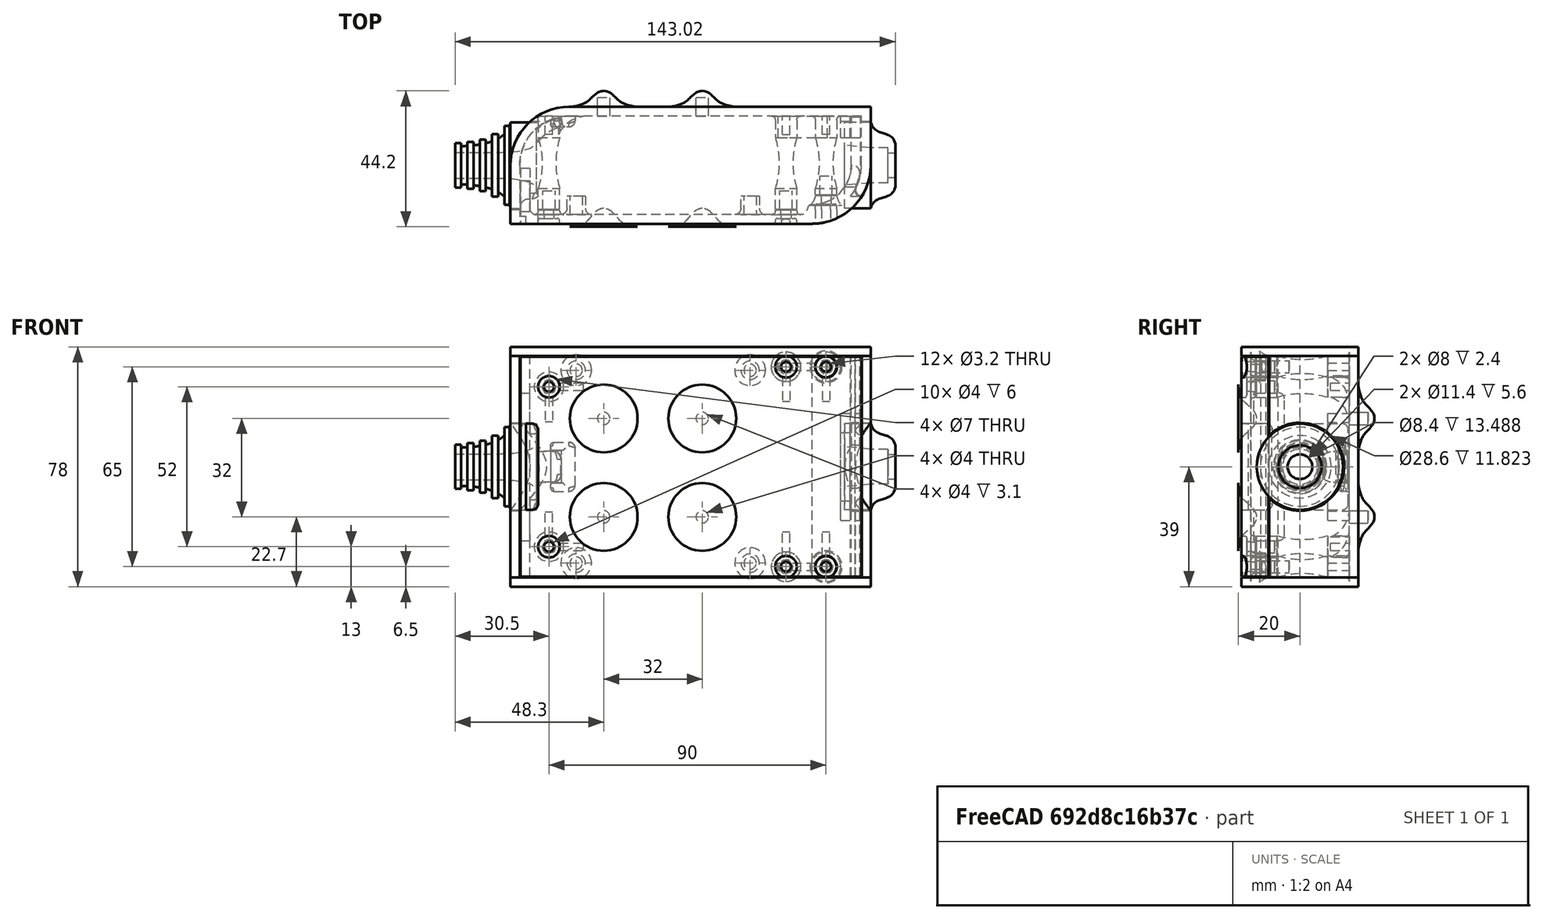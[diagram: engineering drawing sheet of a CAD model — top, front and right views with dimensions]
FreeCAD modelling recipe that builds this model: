
FCSTD DOCUMENT  (FreeCAD 0.19R0.19.2)
Label: enclosure_095
License: All rights reserved
LicenseURL: http://en.wikipedia.org/wiki/All_rights_reserved
objects: Part::Feature×72, Part::Revolution×72, Part::MultiFuse×52, Sketcher::SketchObject×29, Part::Fillet×22, Part::Cylinder×22, Part::Cut×19, Part::Extrusion×18, Part::Box×12, App::MeasureDistance×3
note: 318 computed .brp shape members not serialized (recipe doc carries the construction recipe); baked Part::Feature solids carry a one-line shape summary decoded from their .brp

FEATURE [Sketcher::SketchObject] Sketch  label="topSketch"
  FullyConstrained = true
  sketch-geometry (13):
    g0: LineSegment StartX=117 StartY=19 StartZ=0 EndX=117 EndY=38 EndZ=0
    g1: ArcOfCircle CenterX=98 CenterY=19 CenterZ=0 NormalX=0 NormalY=0 NormalZ=1 AngleXU=0 Radius=19 StartAngle=5.7297 EndAngle=6.28319
    g2: LineSegment StartX=0 StartY=3 StartZ=0 EndX=0 EndY=19 EndZ=0
    g3: LineSegment StartX=19 StartY=38 StartZ=0 EndX=117 EndY=38 EndZ=0
    g4: ArcOfCircle CenterX=19 CenterY=19 CenterZ=0 NormalX=0 NormalY=0 NormalZ=1 AngleXU=0 Radius=19 StartAngle=1.5708 EndAngle=3.14159
    g5: ArcOfCircle CenterX=19 CenterY=19 CenterZ=0 NormalX=0 NormalY=0 NormalZ=1 AngleXU=0 Radius=16 StartAngle=1.5708 EndAngle=3.14159
    g6: ArcOfCircle CenterX=98 CenterY=19 CenterZ=0 NormalX=0 NormalY=0 NormalZ=1 AngleXU=0 Radius=16 StartAngle=5.60905 EndAngle=6.28319
    g7: LineSegment StartX=114 StartY=19 StartZ=0 EndX=114 EndY=35 EndZ=0
    g8: LineSegment StartX=110.5 StartY=9.01251 StartZ=0 EndX=114.163 EndY=9.01251 EndZ=0
    g9: LineSegment StartX=114 StartY=35 StartZ=0 EndX=19 EndY=35 EndZ=0
    g10: LineSegment StartX=0 StartY=3 StartZ=0 EndX=0 EndY=0 EndZ=0
    g11: LineSegment StartX=3 StartY=0 StartZ=0 EndX=0 EndY=0 EndZ=0
    g12: LineSegment StartX=3 StartY=19 StartZ=0 EndX=3 EndY=0 EndZ=0
  constraints (33):
    c: Vertical(g0)
    c: Distance(g0) = 19
    c: Block(g0)
    c: Coincident(g1,g0)
    c: Block(g1)
    c: Vertical(g2)
    c: Block(g2)
    c: Coincident(g3,g0)
    c: Horizontal(g3)
    c: Distance(g3) = 98
    c: Coincident(g4,g3)
    c: Coincident(g4,g2)
    c: Block(g4)
    c: Coincident(g5,g4)
    c: Coincident(g6,g1)
    c: Block(g6)
    c: Block(g5)
    c: Coincident(g7,g6)
    c: Vertical(g7)
    c: Coincident(g8,g6)
    c: Coincident(g8,g1)
    c: Coincident(g9,g7)
    c: Coincident(g9,g5)
    c: Horizontal(g9)
    c: Tangent(g9,g5)
    c: Coincident(g10,g2)
    c: Distance(g10) = 3
    c: Vertical(g10)
    c: Coincident(g11,g10)
    c: Horizontal(g11)
    c: Coincident(g12,g5)
    c: Coincident(g12,g11)
    c: Vertical(g12)
FEATURE [Sketcher::SketchObject] Sketch001  label="bottomSketch"
  FullyConstrained = true
  sketch-geometry (32):
    g0: LineSegment StartX=3.3 StartY=-6.03275e-07 StartZ=0 EndX=98 EndY=-6.03275e-07 EndZ=0
    g1: ArcOfCircle CenterX=98 CenterY=19 CenterZ=0 NormalX=0 NormalY=0 NormalZ=1 AngleXU=0 Radius=19 StartAngle=4.71239 EndAngle=5.71103
    g2: LineSegment StartX=6.3 StartY=8 StartZ=0 EndX=3.3 EndY=8 EndZ=0
    g3: LineSegment StartX=3.3 StartY=8 StartZ=0 EndX=3.3 EndY=-6.03275e-07 EndZ=0
    g4: ArcOfCircle CenterX=8.3 CenterY=5 CenterZ=0 NormalX=0 NormalY=0 NormalZ=1 AngleXU=0 Radius=2 StartAngle=3.14159 EndAngle=4.71239
    g5: LineSegment StartX=6.3 StartY=8 StartZ=0 EndX=6.3 EndY=5 EndZ=0
    g6: ArcOfCircle CenterX=98 CenterY=19 CenterZ=0 NormalX=0 NormalY=0 NormalZ=1 AngleXU=0 Radius=12.7 StartAngle=4.71239 EndAngle=6.28319
    g7: LineSegment StartX=94.7 StartY=3 StartZ=0 EndX=8.3 EndY=3 EndZ=0
    g8-g12: Circle x5 (B-spline internal-alignment scaffolding for g13; pole/knot coordinates omitted)
    g13: BSplineCurve PolesCount=5 KnotsCount=3 Degree=3 IsPeriodic=0
    g14: GeomPoint X=98 Y=6.3 Z=0
    g15: GeomPoint X=96.3938 Y=4.71946 Z=0
    g16: GeomPoint X=94.7 Y=3 Z=0
    g17-g23: Circle x7 (B-spline internal-alignment scaffolding for g24; pole/knot coordinates omitted)
    g24: BSplineCurve PolesCount=7 KnotsCount=5 Degree=3 IsPeriodic=0
    g25-g29: GeomPoint x5 (B-spline internal-alignment scaffolding for g24; pole/knot coordinates omitted)
    g30: ArcOfCircle CenterX=98 CenterY=19 CenterZ=0 NormalX=0 NormalY=0 NormalZ=1 AngleXU=0 Radius=15.7 StartAngle=5.81226 EndAngle=6.28319
    g31: LineSegment StartX=110.7 StartY=19 StartZ=0 EndX=113.7 EndY=19 EndZ=0
  constraints (41):
    c: Horizontal(g0)
    c: Coincident(g1,g0)
    c: Block(g1)
    c: Horizontal(g2)
    c: Distance(g2) = 3
    c: Coincident(g3,g2)
    c: Vertical(g3)
    c: Coincident(g3,g0)
    c: Block(g4)
    c: Block(g2)
    c: Coincident(g5,g2)
    c: Coincident(g5,g4)
    c: Vertical(g5)
    c: Coincident(g6,g1)
    c: Block(g6)
    c: Coincident(g7,g4)
    c: Horizontal(g7)
    c: Block(g0)
    c: Block(g7)
    c: Block(g3)
    c: Coincident(g13,g6)
    c: Weight(g8) = 1
    c: Equal(g8, g9-g12) x4
    c: Coincident(g13,g7)
    c: InternalAlignment(g8-g12 -> g13) x5
    c: InternalAlignment(g14,g13)
    c: InternalAlignment(g15,g13)
    c: InternalAlignment(g16,g13)
    c: Block(g13)
    c: Weight(g17) = 1
    c: Equal(g17, g18-g23) x6
    c: Coincident(g24,g1)
    c: InternalAlignment(g17-g23 -> g24) x7
    c: InternalAlignment(g25-g29 -> g24) x5
    c: Block(g24)
    c: Coincident(g30,g24)
    c: Coincident(g31,g6)
    c: Coincident(g31,g30)
    c: Horizontal(g31)
    c: Block(g31)
    c: Block(g30)
FEATURE [Part::Extrusion] Extrude  label="top"
  Base = -> Sketch
  Dir = (0,0,1)
  DirMode = 2
  FaceMakerClass = Part::FaceMakerBullseye
  LengthFwd = 72
  LengthRev = 0
  Solid = true
  Symmetric = false
FEATURE [Part::Extrusion] Extrude001  label="bottom"
  Base = -> Sketch001
  Dir = (0,0,1)
  DirMode = 2
  FaceMakerClass = Part::FaceMakerBullseye
  LengthFwd = 71.4
  LengthRev = 0
  Placement = pos=(0,0,0.3) rot=(0,0,1;0rad)
  Solid = true
  Symmetric = false
FEATURE [Sketcher::SketchObject] Sketch002  label="topSketch001"
  FullyConstrained = true
  sketch-geometry (6):
    g0: LineSegment StartX=19 StartY=38 StartZ=0 EndX=117 EndY=38 EndZ=0
    g1: ArcOfCircle CenterX=19 CenterY=19 CenterZ=0 NormalX=0 NormalY=0 NormalZ=1 AngleXU=0 Radius=19 StartAngle=1.5708 EndAngle=3.14159
    g2: LineSegment StartX=117 StartY=38 StartZ=0 EndX=117 EndY=19 EndZ=0
    g3: LineSegment StartX=98 StartY=1.0161e-12 StartZ=0 EndX=5.22862e-06 EndY=1.0161e-12 EndZ=0
    g4: LineSegment StartX=5.22862e-06 StartY=19 StartZ=0 EndX=5.22862e-06 EndY=1.0161e-12 EndZ=0
    g5: ArcOfCircle CenterX=98 CenterY=19 CenterZ=0 NormalX=0 NormalY=0 NormalZ=1 AngleXU=0 Radius=19 StartAngle=4.71239 EndAngle=6.28319
  constraints (16):
    c: Horizontal(g0)
    c: Distance(g0) = 98
    c: Coincident(g1,g0)
    c: Block(g1)
    c: Coincident(g2,g0)
    c: Vertical(g2)
    c: Distance(g2) = 19
    c: Horizontal(g3)
    c: Coincident(g4,g1)
    c: Vertical(g4)
    c: Coincident(g3,g4)
    c: Block(g3)
    c: Coincident(g5,g2)
    c: Coincident(g5,g3)
    c: Block(g0)
    c: Block(g5)
FEATURE [Part::Extrusion] Extrude002  label="sideA"
  Base = -> Sketch002
  Dir = (0,0,1)
  DirMode = 2
  FaceMakerClass = Part::FaceMakerBullseye
  LengthFwd = 3
  LengthRev = 0
  Placement = pos=(0,0,-3) rot=(0,0,1;0rad)
  Solid = true
  Symmetric = false
FEATURE [Sketcher::SketchObject] Sketch003  label="topSketch002"
  FullyConstrained = true
  sketch-geometry (6):
    g0: LineSegment StartX=19 StartY=38 StartZ=0 EndX=117 EndY=38 EndZ=0
    g1: ArcOfCircle CenterX=19 CenterY=19 CenterZ=0 NormalX=0 NormalY=0 NormalZ=1 AngleXU=0 Radius=19 StartAngle=1.5708 EndAngle=3.14159
    g2: LineSegment StartX=117 StartY=38 StartZ=0 EndX=117 EndY=19 EndZ=0
    g3: LineSegment StartX=98 StartY=1.0161e-12 StartZ=0 EndX=5.22862e-06 EndY=1.0161e-12 EndZ=0
    g4: LineSegment StartX=5.22862e-06 StartY=19 StartZ=0 EndX=5.22862e-06 EndY=1.0161e-12 EndZ=0
    g5: ArcOfCircle CenterX=98 CenterY=19 CenterZ=0 NormalX=0 NormalY=0 NormalZ=1 AngleXU=0 Radius=19 StartAngle=4.71239 EndAngle=6.28319
  constraints (16):
    c: Horizontal(g0)
    c: Distance(g0) = 98
    c: Coincident(g1,g0)
    c: Block(g1)
    c: Coincident(g2,g0)
    c: Vertical(g2)
    c: Distance(g2) = 19
    c: Horizontal(g3)
    c: Coincident(g4,g1)
    c: Vertical(g4)
    c: Coincident(g3,g4)
    c: Block(g3)
    c: Coincident(g5,g2)
    c: Coincident(g5,g3)
    c: Block(g0)
    c: Block(g5)
FEATURE [Part::Extrusion] Extrude003  label="sideB"
  Base = -> Sketch003
  Dir = (0,0,1)
  DirMode = 2
  FaceMakerClass = Part::FaceMakerBullseye
  LengthFwd = 3
  LengthRev = 0
  Placement = pos=(0,0,72) rot=(0,0,1;0rad)
  Solid = true
  Symmetric = false
FEATURE [Sketcher::SketchObject] Sketch004
  FullyConstrained = true
  MapMode = 3
  Placement = pos=(0,0,0) rot=(1,0,0;1.5708rad)
  Support = -> [Extrude]
  sketch-geometry (8):
    g0: Circle CenterX=80.351 CenterY=-67.6202 CenterZ=0 NormalX=0 NormalY=0 NormalZ=1 AngleXU=0 Radius=2
    g1: Circle CenterX=80.351 CenterY=-67.6202 CenterZ=0 NormalX=0 NormalY=0 NormalZ=1 AngleXU=0 Radius=3
    g2: Circle CenterX=80.351 CenterY=-4.92017 CenterZ=0 NormalX=0 NormalY=0 NormalZ=1 AngleXU=0 Radius=2
    g3: Circle CenterX=80.351 CenterY=-4.92017 CenterZ=0 NormalX=0 NormalY=0 NormalZ=1 AngleXU=0 Radius=3
    g4: Circle CenterX=23.851 CenterY=-4.92017 CenterZ=0 NormalX=0 NormalY=0 NormalZ=1 AngleXU=0 Radius=2
    g5: Circle CenterX=23.851 CenterY=-4.92017 CenterZ=0 NormalX=0 NormalY=0 NormalZ=1 AngleXU=0 Radius=3
    g6: Circle CenterX=23.851 CenterY=-67.6202 CenterZ=0 NormalX=0 NormalY=0 NormalZ=1 AngleXU=0 Radius=2
    g7: Circle CenterX=23.851 CenterY=-67.6202 CenterZ=0 NormalX=0 NormalY=0 NormalZ=1 AngleXU=0 Radius=3
  constraints (8):
    c: Block(g3)
    c: Block(g2)
    c: Block(g1)
    c: Block(g0)
    c: Block(g6)
    c: Block(g7)
    c: Block(g4)
    c: Block(g5)
FEATURE [Part::Extrusion] Extrude004
  Base = -> Sketch004
  Dir = (0,-1,2e-16)
  DirMode = 2
  FaceMakerClass = Part::FaceMakerBullseye
  LengthFwd = 6
  LengthRev = 0
  Placement = pos=(0,9,0) rot=(0,0,1;0rad)
  Solid = true
  Symmetric = false
FEATURE [Sketcher::SketchObject] Sketch005
  FullyConstrained = true
  MapMode = 3
  Placement = pos=(0,0,0) rot=(1,0,0;1.5708rad)
  Support = -> [Extrude]
  sketch-geometry (8):
    g0: Circle CenterX=80.351 CenterY=-67.6202 CenterZ=0 NormalX=0 NormalY=0 NormalZ=1 AngleXU=0 Radius=3
    g1: Circle CenterX=80.351 CenterY=-4.92017 CenterZ=0 NormalX=0 NormalY=0 NormalZ=1 AngleXU=0 Radius=3
    g2: Circle CenterX=23.851 CenterY=-4.92017 CenterZ=0 NormalX=0 NormalY=0 NormalZ=1 AngleXU=0 Radius=3
    g3: Circle CenterX=23.851 CenterY=-67.6202 CenterZ=0 NormalX=0 NormalY=0 NormalZ=1 AngleXU=0 Radius=3
    g4: Circle CenterX=23.851 CenterY=-67.6202 CenterZ=0 NormalX=0 NormalY=0 NormalZ=1 AngleXU=0 Radius=5
    g5: Circle CenterX=80.351 CenterY=-67.6202 CenterZ=0 NormalX=0 NormalY=0 NormalZ=1 AngleXU=0 Radius=5
    g6: Circle CenterX=23.851 CenterY=-4.92017 CenterZ=0 NormalX=0 NormalY=0 NormalZ=1 AngleXU=0 Radius=5
    g7: Circle CenterX=80.351 CenterY=-4.92017 CenterZ=0 NormalX=0 NormalY=0 NormalZ=1 AngleXU=0 Radius=5
  constraints (8):
    c: Block(g1)
    c: Block(g0)
    c: Block(g3)
    c: Block(g2)
    c: Block(g5)
    c: Block(g4)
    c: Block(g6)
    c: Block(g7)
FEATURE [Part::Extrusion] Extrude005
  Base = -> Sketch005
  Dir = (0,-1,2e-16)
  DirMode = 2
  FaceMakerClass = Part::FaceMakerBullseye
  LengthFwd = 2
  LengthRev = 0
  Solid = true
  Symmetric = false
FEATURE [Sketcher::SketchObject] Sketch006
  FullyConstrained = true
  MapMode = 3
  Placement = pos=(0,0,0) rot=(1,0,0;1.5708rad)
  sketch-geometry (8):
    g0: Circle CenterX=80.351 CenterY=-67.6202 CenterZ=0 NormalX=0 NormalY=0 NormalZ=1 AngleXU=0 Radius=3
    g1: Circle CenterX=80.351 CenterY=-4.92017 CenterZ=0 NormalX=0 NormalY=0 NormalZ=1 AngleXU=0 Radius=3
    g2: Circle CenterX=23.851 CenterY=-4.92017 CenterZ=0 NormalX=0 NormalY=0 NormalZ=1 AngleXU=0 Radius=3
    g3: Circle CenterX=23.851 CenterY=-67.6202 CenterZ=0 NormalX=0 NormalY=0 NormalZ=1 AngleXU=0 Radius=3
    g4: Circle CenterX=23.851 CenterY=-67.6202 CenterZ=0 NormalX=0 NormalY=0 NormalZ=1 AngleXU=0 Radius=5
    g5: Circle CenterX=80.351 CenterY=-67.6202 CenterZ=0 NormalX=0 NormalY=0 NormalZ=1 AngleXU=0 Radius=5
    g6: Circle CenterX=23.851 CenterY=-4.92017 CenterZ=0 NormalX=0 NormalY=0 NormalZ=1 AngleXU=0 Radius=5
    g7: Circle CenterX=80.351 CenterY=-4.92017 CenterZ=0 NormalX=0 NormalY=0 NormalZ=1 AngleXU=0 Radius=5
  constraints (8):
    c: Block(g1)
    c: Block(g0)
    c: Block(g3)
    c: Block(g2)
    c: Block(g5)
    c: Block(g4)
    c: Block(g6)
    c: Block(g7)
FEATURE [Part::Extrusion] Extrude007
  Base = -> Sketch006
  Dir = (0,-1,2e-16)
  DirMode = 2
  FaceMakerClass = Part::FaceMakerBullseye
  LengthFwd = 2
  LengthRev = 0
  Solid = true
  Symmetric = false
FEATURE [Part::Fillet] Fillet
  Base = -> Extrude007
  Edges = 4 edges r=1.99: [Edge6,Edge12,Edge18,Edge24]
FEATURE [Part::Cut] Cut
  Base = -> Extrude005
  Placement = pos=(0,5,0) rot=(0,0,1;0rad)
  Tool = -> Fillet
FEATURE [Part::MultiFuse] Fusion  label="pCBScrews"
  Placement = pos=(-2.5,0,72.3) rot=(0,0,1;0rad)
  Shapes = -> [Extrude004,Cut]
FEATURE [App::MeasureDistance] Distance  label="Distance: 0.69 mm"
  Distance = 0.685967
  P1 = (24.0138,2.9647,0.3)
  P2 = (23.8901,3,-0.373787)
FEATURE [App::MeasureDistance] Distance001  label="Distance: 0.53 mm"
  Distance = 0.533607
  P1 = (80.2939,3,72.2334)
  P2 = (80.281,2.99661,71.7)
FEATURE [Part::Fillet] Fillet001
  Base = -> Extrude001
  Edges = 1 edges r=2.4: [Edge17]
FEATURE [Part::Fillet] Fillet002  label="bottom001"
  Base = -> Fillet001
  Edges = 1 edges r=2.4: [Edge36]
FEATURE [Part::Fillet] Fillet003  label="top001"
  Base = -> Extrude
  Edges = 1 edges r=2: [Edge1]
FEATURE [Sketcher::SketchObject] Sketch007
  FullyConstrained = true
  sketch-geometry (16):
    g0: LineSegment StartX=4 StartY=0 StartZ=0 EndX=4 EndY=2.4 EndZ=0
    g1: LineSegment StartX=4 StartY=2.4 StartZ=0 EndX=7 EndY=2.4 EndZ=0
    g2: LineSegment StartX=4 StartY=0 StartZ=0 EndX=5.7 EndY=0 EndZ=0
    g3: LineSegment StartX=5.7 StartY=0 StartZ=0 EndX=5.7 EndY=-5.6 EndZ=0
    g4-g8: Circle x5 (B-spline internal-alignment scaffolding for g9; pole/knot coordinates omitted)
    g9: BSplineCurve PolesCount=5 KnotsCount=3 Degree=3 IsPeriodic=0
    g10: GeomPoint X=7 Y=2.4 Z=0
    g11: GeomPoint X=10.4582 Y=-1.55472 Z=0
    g12: GeomPoint X=14 Y=-5.6 Z=0
    g13: LineSegment StartX=14 StartY=-5.6 StartZ=0 EndX=14 EndY=-14.1 EndZ=0
    g14: LineSegment StartX=14 StartY=-14.1 StartZ=0 EndX=6.5 EndY=-14.1 EndZ=0
    g15: LineSegment StartX=5.7 StartY=-5.6 StartZ=0 EndX=6.5 EndY=-14.1 EndZ=0
  constraints (28):
    c: Distance(g0) = 2.4
    c: Vertical(g0)
    c: Block(g0)
    c: Coincident(g1,g0)
    c: Horizontal(g1)
    c: Distance(g1) = 3
    c: Coincident(g2,g0)
    c: Horizontal(g2)
    c: Distance(g2) = 1.7
    c: Coincident(g3,g2)
    c: Vertical(g3)
    c: Distance(g3) = 5.6
    c: Coincident(g9,g1)
    c: Weight(g4) = 1
    c: Equal(g4, g5-g8) x4
    c: InternalAlignment(g4-g8 -> g9) x5
    c: InternalAlignment(g10,g9)
    c: InternalAlignment(g11,g9)
    c: InternalAlignment(g12,g9)
    c: Block(g9)
    c: Coincident(g13,g9)
    c: Vertical(g13)
    c: Distance(g13) = 8.5
    c: Coincident(g14,g13)
    c: Horizontal(g14)
    c: Distance(g14) = 7.5
    c: Coincident(g15,g3)
    c: Coincident(g15,g14)
FEATURE [Part::Feature] Face
  shape: bbox 10 x 16.5 x 2e-07 mm, 1 faces, 0 solids (baked)
FEATURE [Part::Revolution] Revolve  label="plugHousing"
  Angle = 360
  Axis = (0,1,0)
  Base = (0,0,0)
  FaceMakerClass = Part::FaceMakerBullseye
  Placement = pos=(0,0,36.15) rot=(0,0,1;0rad)
  Solid = false
  Source = -> Face
  Symmetric = false
FEATURE [Part::Feature] Face001
  shape: bbox 10 x 16.5 x 2e-07 mm, 1 faces, 0 solids (baked)
FEATURE [Part::Revolution] Revolve001  label="plugHousing001"
  Angle = 360
  Axis = (0,1,0)
  Base = (0,0,0)
  FaceMakerClass = Part::FaceMakerBullseye
  Placement = pos=(0,0,36.15) rot=(0,0,1;0rad)
  Solid = false
  Source = -> Face001
  Symmetric = false
FEATURE [Part::MultiFuse] Fusion001  label="plugHousing002"
  Placement = pos=(0,0,0) rot=(0,0,1;1.5708rad)
  Shapes = -> [Revolve001,Revolve]
FEATURE [Part::Feature] Face002
  shape: bbox 10 x 16.5 x 2e-07 mm, 1 faces, 0 solids (baked)
FEATURE [Part::Revolution] Revolve003  label="plugHousing005"
  Angle = 360
  Axis = (0,1,0)
  Base = (0,0,0)
  FaceMakerClass = Part::FaceMakerBullseye
  Placement = pos=(0,0,36.15) rot=(0,0,1;0rad)
  Solid = false
  Source = -> Face002
  Symmetric = false
FEATURE [Part::Feature] Face003
  shape: bbox 10 x 16.5 x 2e-07 mm, 1 faces, 0 solids (baked)
FEATURE [Part::Revolution] Revolve002  label="plugHousing003"
  Angle = 360
  Axis = (0,1,0)
  Base = (0,0,0)
  FaceMakerClass = Part::FaceMakerBullseye
  Placement = pos=(0,0,36.15) rot=(0,0,1;0rad)
  Solid = false
  Source = -> Face003
  Symmetric = false
FEATURE [Part::MultiFuse] Fusion002  label="plugHousing004"
  Placement = pos=(0,0,0) rot=(0,0,1;1.5708rad)
  Shapes = -> [Revolve002,Revolve003]
FEATURE [Part::MultiFuse] Fusion003  label="plugHousing006"
  Placement = pos=(0,19,0) rot=(0,0,1;3.14159rad)
  Shapes = -> [Fusion002,Fusion001]
FEATURE [Part::Feature] Face004
  shape: bbox 10 x 16.5 x 2e-07 mm, 1 faces, 0 solids (baked)
FEATURE [Part::Revolution] Revolve006  label="plugHousing010"
  Angle = 360
  Axis = (0,1,0)
  Base = (0,0,0)
  FaceMakerClass = Part::FaceMakerBullseye
  Placement = pos=(0,0,36.15) rot=(0,0,1;0rad)
  Solid = false
  Source = -> Face004
  Symmetric = false
FEATURE [Part::Feature] Face005
  shape: bbox 10 x 16.5 x 2e-07 mm, 1 faces, 0 solids (baked)
FEATURE [Part::Revolution] Revolve007  label="plugHousing011"
  Angle = 360
  Axis = (0,1,0)
  Base = (0,0,0)
  FaceMakerClass = Part::FaceMakerBullseye
  Placement = pos=(0,0,36.15) rot=(0,0,1;0rad)
  Solid = false
  Source = -> Face005
  Symmetric = false
FEATURE [Part::Feature] Face006
  shape: bbox 10 x 16.5 x 2e-07 mm, 1 faces, 0 solids (baked)
FEATURE [Part::Revolution] Revolve004  label="plugHousing007"
  Angle = 360
  Axis = (0,1,0)
  Base = (0,0,0)
  FaceMakerClass = Part::FaceMakerBullseye
  Placement = pos=(0,0,36.15) rot=(0,0,1;0rad)
  Solid = false
  Source = -> Face006
  Symmetric = false
FEATURE [Part::MultiFuse] Fusion004  label="plugHousing009"
  Placement = pos=(0,0,0) rot=(0,0,1;1.5708rad)
  Shapes = -> [Revolve004,Revolve007]
FEATURE [Part::Feature] Face007
  shape: bbox 10 x 16.5 x 2e-07 mm, 1 faces, 0 solids (baked)
FEATURE [Part::Revolution] Revolve005  label="plugHousing008"
  Angle = 360
  Axis = (0,1,0)
  Base = (0,0,0)
  FaceMakerClass = Part::FaceMakerBullseye
  Placement = pos=(0,0,36.15) rot=(0,0,1;0rad)
  Solid = false
  Source = -> Face007
  Symmetric = false
FEATURE [Part::MultiFuse] Fusion005  label="plugHousing012"
  Placement = pos=(0,0,0) rot=(0,0,1;1.5708rad)
  Shapes = -> [Revolve006,Revolve005]
FEATURE [Part::MultiFuse] Fusion006  label="plugHousing013"
  Placement = pos=(0,19,0) rot=(0,0,1;3.14159rad)
  Shapes = -> [Fusion005,Fusion004]
FEATURE [Part::MultiFuse] Fusion007  label="plugHousing014"
  Placement = pos=(122.621,0,-0.15) rot=(0,0,1;0rad)
  Shapes = -> [Fusion003,Fusion006]
FEATURE [Part::Cylinder] Cylinder002
  Angle = 360
  AttacherType = Attacher::AttachEngine3D
  Height = 20
  Placement = pos=(0,0,36.15) rot=(0,0,1;0rad)
  Radius = 4
FEATURE [Part::Cylinder] Cylinder003
  Angle = 360
  AttacherType = Attacher::AttachEngine3D
  Height = 10
  Placement = pos=(0,0,36.15) rot=(0,0,1;0rad)
  Radius = 4
FEATURE [Part::MultiFuse] Fusion009  label="removeToCreateHoleForPlugHousing"
  Placement = pos=(70,19,36.15) rot=(0,1,0;1.5708rad)
  Shapes = -> [Cylinder002,Cylinder003]
FEATURE [Part::Cylinder] Cylinder004
  Angle = 360
  AttacherType = Attacher::AttachEngine3D
  Height = 20
  Placement = pos=(0,0,36.15) rot=(0,0,1;0rad)
  Radius = 4
FEATURE [Part::Cylinder] Cylinder005
  Angle = 360
  AttacherType = Attacher::AttachEngine3D
  Height = 10
  Placement = pos=(0,0,36.15) rot=(0,0,1;0rad)
  Radius = 4
FEATURE [Part::MultiFuse] Fusion010  label="removeToCreateHoleForPlugHousing001"
  Placement = pos=(70,19,36.15) rot=(0,1,0;1.5708rad)
  Shapes = -> [Cylinder004,Cylinder005]
FEATURE [Part::Cut] Cut001
  Base = -> Fillet003
  Tool = -> Fusion010
FEATURE [Part::Cut] Cut002  label="Bottom"
  Base = -> Fillet002
  Tool = -> Fusion009
FEATURE [Part::Feature] Face008
  shape: bbox 10 x 16.5 x 2e-07 mm, 1 faces, 0 solids (baked)
FEATURE [Part::Revolution] Revolve011  label="plugHousing021"
  Angle = 360
  Axis = (0,1,0)
  Base = (0,0,0)
  FaceMakerClass = Part::FaceMakerBullseye
  Placement = pos=(0,0,36.15) rot=(0,0,1;0rad)
  Solid = false
  Source = -> Face008
  Symmetric = false
FEATURE [Part::Feature] Face009
  shape: bbox 10 x 16.5 x 2e-07 mm, 1 faces, 0 solids (baked)
FEATURE [Part::Revolution] Revolve012  label="plugHousing022"
  Angle = 360
  Axis = (0,1,0)
  Base = (0,0,0)
  FaceMakerClass = Part::FaceMakerBullseye
  Placement = pos=(0,0,36.15) rot=(0,0,1;0rad)
  Solid = false
  Source = -> Face009
  Symmetric = false
FEATURE [Part::Feature] Face010 .. Face013  x4 (patterned run collapsed; names and placements below)
  shape: bbox 10 x 16.5 x 2e-07 mm, 1 faces, 0 solids (baked)
FEATURE [Part::Revolution] Revolve015  label="plugHousing027"
  Angle = 360
  Axis = (0,1,0)
  Base = (0,0,0)
  FaceMakerClass = Part::FaceMakerBullseye
  Placement = pos=(0,0,36.15) rot=(0,0,1;0rad)
  Solid = false
  Source = -> Face013
  Symmetric = false
FEATURE [Part::Feature] Face014
  shape: bbox 10 x 16.5 x 2e-07 mm, 1 faces, 0 solids (baked)
FEATURE [Part::Feature] Face015
  shape: bbox 10 x 16.5 x 2e-07 mm, 1 faces, 0 solids (baked)
FEATURE [Part::Feature] Face016
  shape: bbox 10 x 16.5 x 2e-07 mm, 1 faces, 0 solids (baked)
FEATURE [Part::Revolution] Revolve019  label="plugHousing033"
  Angle = 360
  Axis = (0,1,0)
  Base = (0,0,0)
  FaceMakerClass = Part::FaceMakerBullseye
  Placement = pos=(0,0,36.15) rot=(0,0,1;0rad)
  Solid = false
  Source = -> Face016
  Symmetric = false
FEATURE [Part::Feature] Face017
  shape: bbox 10 x 16.5 x 2e-07 mm, 1 faces, 0 solids (baked)
FEATURE [Part::Revolution] Revolve020  label="plugHousing034"
  Angle = 360
  Axis = (0,1,0)
  Base = (0,0,0)
  FaceMakerClass = Part::FaceMakerBullseye
  Placement = pos=(0,0,36.15) rot=(0,0,1;0rad)
  Solid = false
  Source = -> Face017
  Symmetric = false
FEATURE [Part::Feature] Face018
  shape: bbox 10 x 16.5 x 2e-07 mm, 1 faces, 0 solids (baked)
FEATURE [Part::Revolution] Revolve016  label="plugHousing030"
  Angle = 360
  Axis = (0,1,0)
  Base = (0,0,0)
  FaceMakerClass = Part::FaceMakerBullseye
  Placement = pos=(0,0,36.15) rot=(0,0,1;0rad)
  Solid = false
  Source = -> Face018
  Symmetric = false
FEATURE [Part::MultiFuse] Fusion020  label="plugHousing038"
  Placement = pos=(0,0,0) rot=(0,0,1;1.5708rad)
  Shapes = -> [Revolve016,Revolve020]
FEATURE [Part::Feature] Face019
  shape: bbox 10 x 16.5 x 2e-07 mm, 1 faces, 0 solids (baked)
FEATURE [Part::Feature] Face020
  shape: bbox 10 x 16.5 x 2e-07 mm, 1 faces, 0 solids (baked)
FEATURE [Part::Revolution] Revolve017  label="plugHousing031"
  Angle = 360
  Axis = (0,1,0)
  Base = (0,0,0)
  FaceMakerClass = Part::FaceMakerBullseye
  Placement = pos=(0,0,36.15) rot=(0,0,1;0rad)
  Solid = false
  Source = -> Face020
  Symmetric = false
FEATURE [Part::MultiFuse] Fusion021  label="plugHousing039"
  Placement = pos=(0,0,0) rot=(0,0,1;1.5708rad)
  Shapes = -> [Revolve019,Revolve017]
FEATURE [Part::MultiFuse] Fusion023  label="plugHousing041"
  Placement = pos=(0,19,0) rot=(0,0,1;3.14159rad)
  Shapes = -> [Fusion021,Fusion020]
FEATURE [Part::Revolution] Revolve022  label="plugHousing043"
  Angle = 360
  Axis = (0,1,0)
  Base = (0,0,0)
  FaceMakerClass = Part::FaceMakerBullseye
  Placement = pos=(0,0,36.15) rot=(0,0,1;0rad)
  Solid = false
  Source = -> Face019
  Symmetric = false
FEATURE [Part::Feature] Face021
  shape: bbox 10 x 16.5 x 2e-07 mm, 1 faces, 0 solids (baked)
FEATURE [Part::Revolution] Revolve023  label="plugHousing044"
  Angle = 360
  Axis = (0,1,0)
  Base = (0,0,0)
  FaceMakerClass = Part::FaceMakerBullseye
  Placement = pos=(0,0,36.15) rot=(0,0,1;0rad)
  Solid = false
  Source = -> Face021
  Symmetric = false
FEATURE [Part::Feature] Face022
  shape: bbox 10 x 16.5 x 2e-07 mm, 1 faces, 0 solids (baked)
FEATURE [Part::Revolution] Revolve018  label="plugHousing032"
  Angle = 360
  Axis = (0,1,0)
  Base = (0,0,0)
  FaceMakerClass = Part::FaceMakerBullseye
  Placement = pos=(0,0,36.15) rot=(0,0,1;0rad)
  Solid = false
  Source = -> Face022
  Symmetric = false
FEATURE [Part::MultiFuse] Fusion022  label="plugHousing040"
  Placement = pos=(0,0,0) rot=(0,0,1;1.5708rad)
  Shapes = -> [Revolve018,Revolve023]
FEATURE [Part::Feature] Face023
  shape: bbox 10 x 16.5 x 2e-07 mm, 1 faces, 0 solids (baked)
FEATURE [Part::Revolution] Revolve021  label="plugHousing035"
  Angle = 360
  Axis = (0,1,0)
  Base = (0,0,0)
  FaceMakerClass = Part::FaceMakerBullseye
  Placement = pos=(0,0,36.15) rot=(0,0,1;0rad)
  Solid = false
  Source = -> Face023
  Symmetric = false
FEATURE [Part::MultiFuse] Fusion018  label="plugHousing036"
  Placement = pos=(0,0,0) rot=(0,0,1;1.5708rad)
  Shapes = -> [Revolve022,Revolve021]
FEATURE [Part::MultiFuse] Fusion019  label="plugHousing037"
  Placement = pos=(0,19,0) rot=(0,0,1;3.14159rad)
  Shapes = -> [Fusion018,Fusion022]
FEATURE [Part::MultiFuse] Fusion024  label="plugHousing042"
  Placement = pos=(122.621,0,-0.15) rot=(0,0,1;0rad)
  Shapes = -> [Fusion023,Fusion019]
FEATURE [Part::Cylinder] Cylinder006
  Angle = 360
  AttacherType = Attacher::AttachEngine3D
  Height = 20
  Placement = pos=(0,0,36.15) rot=(0,0,1;0rad)
  Radius = 14.3
FEATURE [Part::Cylinder] Cylinder007
  Angle = 360
  AttacherType = Attacher::AttachEngine3D
  Height = 10
  Placement = pos=(0,0,36.15) rot=(0,0,1;0rad)
  Radius = 4
FEATURE [Part::MultiFuse] Fusion026  label="removeToCreteHoleForPlugHousing"
  Placement = pos=(70,19,36) rot=(0,1,0;1.5708rad)
  Shapes = -> [Cylinder006,Cylinder007]
FEATURE [Part::Box] Box001  label="Cube001"
  AttacherType = Attacher::AttachEngine3D
  Height = 28
  Length = 3
  Placement = pos=(110.7,19,22) rot=(0,0,1;0rad)
  Width = 15.7
FEATURE [Part::Cut] Cut003  label="top002"
  Base = -> Cut001
  Tool = -> Fusion007
FEATURE [Part::Revolution] Revolve008  label="plugHousing015"
  Angle = 360
  Axis = (0,1,0)
  Base = (0,0,0)
  FaceMakerClass = Part::FaceMakerBullseye
  Placement = pos=(0,0,36.15) rot=(0,0,1;0rad)
  Solid = false
  Source = -> Face010
  Symmetric = false
FEATURE [Part::MultiFuse] Fusion013  label="plugHousing020"
  Placement = pos=(0,0,0) rot=(0,0,1;1.5708rad)
  Shapes = -> [Revolve008,Revolve012]
FEATURE [Part::Cut] Cut004  label="top003"
  Base = -> Cut003
  Placement = pos=(1,0,0) rot=(0,0,1;0rad)
  Tool = -> Fusion026
FEATURE [Part::Cylinder] Cylinder008
  Angle = 360
  AttacherType = Attacher::AttachEngine3D
  Height = 20
  Placement = pos=(0,0,36.15) rot=(0,0,1;0rad)
  Radius = 10.3
FEATURE [Part::Cylinder] Cylinder009
  Angle = 360
  AttacherType = Attacher::AttachEngine3D
  Height = 10
  Placement = pos=(0,0,36.15) rot=(0,0,1;0rad)
  Radius = 4
FEATURE [Part::MultiFuse] Fusion027  label="removeToCreteHoleForPlugHousing001"
  Placement = pos=(70,19,36) rot=(0,1,0;1.5708rad)
  Shapes = -> [Cylinder008,Cylinder009]
FEATURE [Part::Cut] Cut005  label="plugHousingTab"
  Base = -> Box001
  Tool = -> Fusion027
FEATURE [Part::MultiFuse] Fusion028  label="plugHousing045"
  Shapes = -> [Fusion024,Cut005]
FEATURE [Part::Box] Box002  label="Cube002"
  AttacherType = Attacher::AttachEngine3D
  Height = 28.8
  Length = 3
  Placement = pos=(107.3,28,21.6) rot=(0,0,1;0rad)
  Width = 7
FEATURE [Part::Box] Box003  label="Cube003"
  AttacherType = Attacher::AttachEngine3D
  Height = 3
  Length = 6.4
  Placement = pos=(107.3,28,18.6) rot=(0,0,1;0rad)
  Width = 7
FEATURE [Part::Box] Box004  label="Cube004"
  AttacherType = Attacher::AttachEngine3D
  Height = 3
  Length = 6.4
  Placement = pos=(107.3,28,50.4) rot=(0,0,1;0rad)
  Width = 7
FEATURE [Part::MultiFuse] Fusion029  label="plugHousingBracketHolder"
  Shapes = -> [Box004,Box002,Box003]
FEATURE [Part::Cylinder] Cylinder010
  Angle = 360
  AttacherType = Attacher::AttachEngine3D
  Height = 20
  Placement = pos=(0,0,36.15) rot=(0,0,1;0rad)
  Radius = 14.3
FEATURE [Part::Cylinder] Cylinder011
  Angle = 360
  AttacherType = Attacher::AttachEngine3D
  Height = 10
  Placement = pos=(0,0,36.15) rot=(0,0,1;0rad)
  Radius = 4
FEATURE [Part::MultiFuse] Fusion030  label="removeToCreteHoleForPlugHousing002"
  Placement = pos=(70,19,36) rot=(0,1,0;1.5708rad)
  Shapes = -> [Cylinder010,Cylinder011]
FEATURE [Part::Cut] Cut006  label="plugHousingBracketHolder001"
  Base = -> Fusion029
  Tool = -> Fusion030
FEATURE [Part::Cylinder] Cylinder012
  Angle = 360
  AttacherType = Attacher::AttachEngine3D
  Height = 20
  Placement = pos=(0,0,36.15) rot=(0,0,1;0rad)
  Radius = 7
FEATURE [Part::Cylinder] Cylinder013
  Angle = 360
  AttacherType = Attacher::AttachEngine3D
  Height = 10
  Placement = pos=(0,0,36.15) rot=(0,0,1;0rad)
  Radius = 4
FEATURE [Part::MultiFuse] Fusion032  label="removeToCreteHoleForPlugHousing003"
  Placement = pos=(70,19,36) rot=(0,1,0;1.5708rad)
  Shapes = -> [Cylinder012,Cylinder013]
FEATURE [Part::Cut] Cut007  label="bottom002"
  Base = -> Cut002
  Tool = -> Fusion032
FEATURE [Sketcher::SketchObject] Sketch008
  FullyConstrained = true
  sketch-geometry (54):
    g0: LineSegment StartX=-4.2 StartY=0 StartZ=0 EndX=-6.2 EndY=0 EndZ=0
    g1: LineSegment StartX=-14 StartY=-18 StartZ=0 EndX=-14 EndY=-26.5 EndZ=0
    g2: LineSegment StartX=-4.2 StartY=0 StartZ=0 EndX=-4.2 EndY=-13.4877 EndZ=0
    g3: Circle CenterX=-4.2 CenterY=-13.4877 CenterZ=0 NormalX=0 NormalY=0 NormalZ=1 AngleXU=0 Radius=1
    g4: Circle CenterX=-4.2 CenterY=-26.5 CenterZ=0 NormalX=0 NormalY=0 NormalZ=1 AngleXU=0 Radius=1
    g5: Circle CenterX=-8.2 CenterY=-26.5 CenterZ=0 NormalX=0 NormalY=0 NormalZ=1 AngleXU=0 Radius=1
    g6: BSplineCurve PolesCount=3 KnotsCount=2 Degree=2 IsPeriodic=0
    g7: GeomPoint X=-4.2 Y=-13.4877 Z=0
    g8: GeomPoint X=-8.2 Y=-26.5 Z=0
    g9: LineSegment StartX=-14 StartY=-26.5 StartZ=0 EndX=-8.2 EndY=-26.5 EndZ=0
    g10: LineSegment StartX=-10.15 StartY=-12 StartZ=0 EndX=-10.15 EndY=-14 EndZ=0
    g11: LineSegment StartX=-12.8401 StartY=-16 StartZ=0 EndX=-10.1571 EndY=-16 EndZ=0
    g12: LineSegment StartX=-10.15 StartY=-14 StartZ=0 EndX=-8.70761 EndY=-14 EndZ=0
    g13: LineSegment StartX=-12.8401 StartY=-16 StartZ=0 EndX=-12.8401 EndY=-17.6958 EndZ=0
    g14: LineSegment StartX=-10.15 StartY=-12 StartZ=0 EndX=-7.79258 EndY=-12 EndZ=0
    g15: Circle CenterX=-6.2215 CenterY=-2 CenterZ=0 NormalX=0 NormalY=0 NormalZ=1 AngleXU=0 Radius=1
    g16: Circle CenterX=-6.22762 CenterY=-2.58724 CenterZ=0 NormalX=0 NormalY=0 NormalZ=1 AngleXU=0 Radius=1
    g17: Circle CenterX=-6.32538 CenterY=-4 CenterZ=0 NormalX=0 NormalY=0 NormalZ=1 AngleXU=0 Radius=1
    g18: BSplineCurve PolesCount=3 KnotsCount=2 Degree=2 IsPeriodic=0
    g19: GeomPoint X=-6.2215 Y=-2 Z=0
    g20: GeomPoint X=-6.32538 Y=-4 Z=0
    g21: Circle CenterX=-6.48644 CenterY=-5.99526 CenterZ=0 NormalX=0 NormalY=0 NormalZ=1 AngleXU=0 Radius=1
    g22: Circle CenterX=-6.58486 CenterY=-6.99526 CenterZ=0 NormalX=0 NormalY=0 NormalZ=1 AngleXU=0 Radius=1
    g23: Circle CenterX=-6.77343 CenterY=-8 CenterZ=0 NormalX=0 NormalY=0 NormalZ=1 AngleXU=0 Radius=1
    g24: BSplineCurve PolesCount=3 KnotsCount=2 Degree=2 IsPeriodic=0
    g25: GeomPoint X=-6.48644 Y=-5.99526 Z=0
    g26: GeomPoint X=-6.77343 Y=-8 Z=0
    g27: Circle CenterX=-7.19003 CenterY=-10 CenterZ=0 NormalX=0 NormalY=0 NormalZ=1 AngleXU=0 Radius=1
    g28: Circle CenterX=-7.44407 CenterY=-11.0915 CenterZ=0 NormalX=0 NormalY=0 NormalZ=1 AngleXU=0 Radius=1
    g29: Circle CenterX=-7.79258 CenterY=-12 CenterZ=0 NormalX=0 NormalY=0 NormalZ=1 AngleXU=0 Radius=1
    g30: BSplineCurve PolesCount=3 KnotsCount=2 Degree=2 IsPeriodic=0
    g31: GeomPoint X=-7.19003 Y=-10 Z=0
    g32: GeomPoint X=-7.79258 Y=-12 Z=0
    g33: Circle CenterX=-8.70761 CenterY=-14 CenterZ=0 NormalX=0 NormalY=0 NormalZ=1 AngleXU=0 Radius=1
    g34: Circle CenterX=-9.33087 CenterY=-15.1837 CenterZ=0 NormalX=0 NormalY=0 NormalZ=1 AngleXU=0 Radius=1
    g35: Circle CenterX=-10.1571 CenterY=-16 CenterZ=0 NormalX=0 NormalY=0 NormalZ=1 AngleXU=0 Radius=1
    g36: BSplineCurve PolesCount=3 KnotsCount=2 Degree=2 IsPeriodic=0
    g37: GeomPoint X=-8.70761 Y=-14 Z=0
    g38: GeomPoint X=-10.1571 Y=-16 Z=0
    g39: Circle CenterX=-12.8401 CenterY=-17.6958 CenterZ=0 NormalX=0 NormalY=0 NormalZ=1 AngleXU=0 Radius=1
    g40: Circle CenterX=-13.3521 CenterY=-17.9027 CenterZ=0 NormalX=0 NormalY=0 NormalZ=1 AngleXU=0 Radius=1
    g41: Circle CenterX=-14 CenterY=-18 CenterZ=0 NormalX=0 NormalY=0 NormalZ=1 AngleXU=0 Radius=1
    g42: BSplineCurve PolesCount=3 KnotsCount=2 Degree=2 IsPeriodic=0
    g43: GeomPoint X=-12.8401 Y=-17.6958 Z=0
    g44: GeomPoint X=-14 Y=-18 Z=0
    g45: LineSegment StartX=-6.2 StartY=0 StartZ=0 EndX=-7.2 EndY=0 EndZ=0
    g46: LineSegment StartX=-7.2 StartY=0 StartZ=0 EndX=-7.2 EndY=-2 EndZ=0
    g47: LineSegment StartX=-7.2 StartY=-2 StartZ=0 EndX=-6.2215 EndY=-2 EndZ=0
    g48: LineSegment StartX=-6.32538 StartY=-4 StartZ=0 EndX=-7.65538 EndY=-4 EndZ=0
    g49: LineSegment StartX=-7.65538 StartY=-4 StartZ=0 EndX=-7.65538 EndY=-5.99526 EndZ=0
    g50: LineSegment StartX=-7.65538 StartY=-5.99526 StartZ=0 EndX=-6.48644 EndY=-5.99526 EndZ=0
    g51: LineSegment StartX=-6.77343 StartY=-8 StartZ=0 EndX=-8.43343 EndY=-8 EndZ=0
    g52: LineSegment StartX=-8.43343 StartY=-8 StartZ=0 EndX=-8.43343 EndY=-10 EndZ=0
    g53: LineSegment StartX=-8.43343 StartY=-10 StartZ=0 EndX=-7.19003 EndY=-10 EndZ=0
  constraints (112):
    c: Horizontal(g0)
    c: Distance(g0) = 2
    c: Block(g0)
    c: Vertical(g1)
    c: Coincident(g2,g0)
    c: Vertical(g2)
    c: Block(g2)
    c: Coincident(g6,g2)
    c: Weight(g3) = 1
    c: Equal(g3,g4)
    c: Equal(g3,g5)
    c: InternalAlignment(g3,g6)
    c: InternalAlignment(g4,g6)
    c: InternalAlignment(g5,g6)
    c: InternalAlignment(g7,g6)
    c: InternalAlignment(g8,g6)
    c: Block(g6)
    c: Coincident(g9,g1)
    c: Coincident(g9,g6)
    c: Horizontal(g9)
    c: Vertical(g10)
    c: Block(g10)
    c: Horizontal(g11)
    c: Block(g11)
    c: Coincident(g12,g10)
    c: Horizontal(g12)
    c: Block(g12)
    c: Coincident(g13,g11)
    c: Vertical(g13)
    c: Block(g13)
    c: Coincident(g14,g10)
    c: Horizontal(g14)
    c: Block(g14)
    c: Block(g9)
    c: Block(g1)
    c: Weight(g15) = 1
    c: Equal(g15,g16)
    c: Equal(g15,g17)
    c: InternalAlignment(g15,g18)
    c: InternalAlignment(g16,g18)
    c: InternalAlignment(g17,g18)
    c: InternalAlignment(g19,g18)
    c: InternalAlignment(g20,g18)
    c: Weight(g21) = 1
    c: Equal(g21,g22)
    c: Equal(g21,g23)
    c: InternalAlignment(g21,g24)
    c: InternalAlignment(g22,g24)
    c: InternalAlignment(g23,g24)
    c: InternalAlignment(g25,g24)
    c: InternalAlignment(g26,g24)
    c: Weight(g27) = 1
    c: Equal(g27,g28)
    c: Equal(g27,g29)
    c: Coincident(g30,g14)
    c: InternalAlignment(g27,g30)
    c: InternalAlignment(g28,g30)
    c: InternalAlignment(g29,g30)
    c: InternalAlignment(g31,g30)
    c: InternalAlignment(g32,g30)
    c: Coincident(g36,g12)
    c: Weight(g33) = 1
    c: Equal(g33,g34)
    c: Equal(g33,g35)
    c: Coincident(g36,g11)
    c: InternalAlignment(g33,g36)
    c: InternalAlignment(g34,g36)
    c: InternalAlignment(g35,g36)
    c: InternalAlignment(g37,g36)
    c: InternalAlignment(g38,g36)
    c: Coincident(g42,g13)
    c: Weight(g39) = 1
    c: Equal(g39,g40)
    c: Equal(g39,g41)
    c: Coincident(g42,g1)
    c: InternalAlignment(g39,g42)
    c: InternalAlignment(g40,g42)
    c: InternalAlignment(g41,g42)
    c: InternalAlignment(g43,g42)
    c: InternalAlignment(g44,g42)
    c: Block(g18)
    c: Block(g24)
    c: Block(g30)
    c: Block(g36)
    c: Block(g42)
    c: Horizontal(g45)
    c: Coincident(g45,g0)
    c: Vertical(g46)
    c: Coincident(g46,g45)
    c: Coincident(g47,g46)
    c: Coincident(g47,g18)
    c: Horizontal(g47)
    c: Block(g46)
    c: Coincident(g48,g18)
    c: Horizontal(g48)
    c: Distance(g48) = 1.33
    c: Vertical(g49)
    c: Coincident(g49,g48)
    c: Coincident(g50,g49)
    c: Coincident(g50,g24)
    c: Horizontal(g50)
    c: Tangent(g50,g22)
    c: Horizontal(g51)
    c: Coincident(g51,g24)
    c: Block(g51)
    c: Vertical(g52)
    c: Block(g52)
    c: Coincident(g52,g51)
    c: Coincident(g53,g52)
    c: Coincident(g53,g30)
    c: Horizontal(g53)
    c: Distance(g1) = 8.5
FEATURE [Part::Feature] Face024
  shape: bbox 9.8 x 26.5 x 2e-07 mm, 1 faces, 0 solids (baked)
FEATURE [Part::Revolution] Revolve024
  Angle = 360
  Axis = (0,1,0)
  Base = (0,0,0)
  FaceMakerClass = Part::FaceMakerBullseye
  Placement = pos=(0,0,0) rot=(0,0,1;1.5708rad)
  Solid = false
  Source = -> Face024
  Symmetric = false
FEATURE [Part::Feature] Face025
  shape: bbox 9.8 x 26.5 x 2e-07 mm, 1 faces, 0 solids (baked)
FEATURE [Part::Revolution] Revolve025
  Angle = 360
  Axis = (0,1,0)
  Base = (0,0,0)
  FaceMakerClass = Part::FaceMakerBullseye
  Placement = pos=(0,0,0) rot=(0,0,1;1.5708rad)
  Solid = false
  Source = -> Face025
  Symmetric = false
FEATURE [Part::MultiFuse] Fusion033
  Placement = pos=(-18,19,36) rot=(0,0,1;0rad)
  Shapes = -> [Revolve025,Revolve024]
FEATURE [Part::Cylinder] Cylinder014
  Angle = 360
  AttacherType = Attacher::AttachEngine3D
  Height = 20
  Placement = pos=(0,0,36.15) rot=(0,0,1;0rad)
  Radius = 14.3
FEATURE [Part::Cylinder] Cylinder015
  Angle = 360
  AttacherType = Attacher::AttachEngine3D
  Height = 10
  Placement = pos=(0,0,36.15) rot=(0,0,1;0rad)
  Radius = 4
FEATURE [Part::MultiFuse] Fusion034  label="removeToCreteHoleForPlugHousing004"
  Placement = pos=(-42,19,36) rot=(0,1,0;1.5708rad)
  Shapes = -> [Cylinder014,Cylinder015]
FEATURE [Part::Cut] Cut008  label="top004"
  Base = -> Cut004
  Placement = pos=(-1,0,0) rot=(0,0,1;0rad)
  Tool = -> Fusion034
FEATURE [Part::Box] Box005  label="Cube005"
  AttacherType = Attacher::AttachEngine3D
  Height = 28
  Length = 3
  Placement = pos=(110.7,19,22) rot=(0,0,1;0rad)
  Width = 15.7
FEATURE [Part::Cylinder] Cylinder016
  Angle = 360
  AttacherType = Attacher::AttachEngine3D
  Height = 10
  Placement = pos=(0,0,36.15) rot=(0,0,1;0rad)
  Radius = 4
FEATURE [Part::Cylinder] Cylinder017
  Angle = 360
  AttacherType = Attacher::AttachEngine3D
  Height = 20
  Placement = pos=(0,0,36.15) rot=(0,0,1;0rad)
  Radius = 10.3
FEATURE [Part::MultiFuse] Fusion035  label="removeToCreteHoleForPlugHousing005"
  Placement = pos=(70,19,36) rot=(0,1,0;1.5708rad)
  Shapes = -> [Cylinder017,Cylinder016]
FEATURE [Part::Cut] Cut009  label="plugHousingTab001"
  Base = -> Box005
  Placement = pos=(-107.4,-14,0) rot=(0,0,1;0rad)
  Tool = -> Fusion035
FEATURE [Part::Box] Box006  label="Cube006"
  AttacherType = Attacher::AttachEngine3D
  Height = 28
  Length = 3
  Placement = pos=(110.7,19,22) rot=(0,0,1;0rad)
  Width = 15.7
FEATURE [Part::Cylinder] Cylinder018
  Angle = 360
  AttacherType = Attacher::AttachEngine3D
  Height = 10
  Placement = pos=(0,0,36.15) rot=(0,0,1;0rad)
  Radius = 4
FEATURE [Part::Cylinder] Cylinder019
  Angle = 360
  AttacherType = Attacher::AttachEngine3D
  Height = 20
  Placement = pos=(0,0,36.15) rot=(0,0,1;0rad)
  Radius = 10.3
FEATURE [Part::MultiFuse] Fusion036  label="removeToCreteHoleForPlugHousing006"
  Placement = pos=(70,19,36) rot=(0,1,0;1.5708rad)
  Shapes = -> [Cylinder019,Cylinder018]
FEATURE [Part::Cut] Cut010  label="plugHousingTab002"
  Base = -> Box006
  Placement = pos=(-107.4,-14,0) rot=(0,0,1;0rad)
  Tool = -> Fusion036
FEATURE [Part::MultiFuse] Fusion037
  Placement = pos=(9.6,23,0) rot=(0,0,1;3.14159rad)
  Shapes = -> [Cut009,Cut010]
FEATURE [Part::Box] Box  label="Cube"
  AttacherType = Attacher::AttachEngine3D
  Height = 10
  Length = 3
  Placement = pos=(3.3,4,12) rot=(0,0,1;0rad)
  Width = 10
FEATURE [Part::Fillet] Fillet004
  Base = -> Fusion028
  Edges = 1 edges r=2: [Edge25]
FEATURE [Part::Fillet] Fillet005  label="plugHousing046"
  Base = -> Fillet004
  Edges = 1 edges r=2: [Edge8]
FEATURE [Part::Fillet] Fillet006
  Base = -> Box
  Edges = 1 edges r=2: [Edge11]
FEATURE [Part::Box] Box007  label="Cube007"
  AttacherType = Attacher::AttachEngine3D
  Height = 10
  Length = 3
  Placement = pos=(3.3,4,50) rot=(0,0,1;0rad)
  Width = 10
FEATURE [Part::Fillet] Fillet007
  Base = -> Box007
  Edges = 1 edges r=2: [Edge12]
FEATURE [Part::Box] Box008  label="Cube008"
  AttacherType = Attacher::AttachEngine3D
  Height = 28
  Length = 4
  Placement = pos=(5,0,22) rot=(0,0,1;0rad)
  Width = 10
FEATURE [Part::Fillet] Fillet008
  Base = -> Box008
  Edges = 1 edges r=1: [Edge7]
FEATURE [Part::Fillet] Fillet009
  Base = -> Fillet008
  Edges = 1 edges r=2: [Edge5]
FEATURE [Part::Fillet] Fillet010
  Base = -> Fillet009
  Edges = 1 edges r=2: [Edge2]
FEATURE [Sketcher::SketchObject] Sketch009  label="topSketch003"
  FullyConstrained = true
  sketch-geometry (4):
    g0: LineSegment StartX=16.8446 StartY=31.512 StartZ=0 EndX=16.3251 EndY=34.4666 EndZ=0
    g1: ArcOfCircle CenterX=19 CenterY=19.2524 CenterZ=0 NormalX=0 NormalY=0 NormalZ=1 AngleXU=0 Radius=15.4476 StartAngle=1.74483 EndAngle=2.72717
    g2: ArcOfCircle CenterX=19 CenterY=19.2524 CenterZ=0 NormalX=0 NormalY=0 NormalZ=1 AngleXU=0 Radius=12.4476 StartAngle=1.74483 EndAngle=2.73189
    g3: LineSegment StartX=4.86004 StartY=25.4725 StartZ=0 EndX=7.58253 EndY=24.2107 EndZ=0
  constraints (7):
    c: Block(g0)
    c: Coincident(g1,g0)
    c: Coincident(g2,g0)
    c: Coincident(g3,g1)
    c: Coincident(g3,g2)
    c: Block(g1)
    c: Block(g2)
FEATURE [Part::Extrusion] Extrude008
  Base = -> Sketch009
  Dir = (0,0,1)
  DirMode = 2
  FaceMakerClass = Part::FaceMakerBullseye
  LengthFwd = 10
  LengthRev = 0
  Placement = pos=(0,0,31) rot=(0,0,1;0rad)
  Solid = true
  Symmetric = false
FEATURE [Part::Cylinder] Cylinder020
  Angle = 360
  AttacherType = Attacher::AttachEngine3D
  Height = 20
  Placement = pos=(0,0,36.15) rot=(0,0,1;0rad)
  Radius = 8.2
FEATURE [Part::Cylinder] Cylinder021
  Angle = 360
  AttacherType = Attacher::AttachEngine3D
  Height = 10
  Placement = pos=(0,0,36.15) rot=(0,0,1;0rad)
  Radius = 4
FEATURE [Part::MultiFuse] Fusion038  label="removeToCreteHoleForPlugHousing007"
  Placement = pos=(-42,19,36) rot=(0,1,0;1.5708rad)
  Shapes = -> [Cylinder020,Cylinder021]
FEATURE [Part::Cut] Cut011
  Base = -> Extrude008
  Tool = -> Fusion038
FEATURE [Part::Fillet] Fillet011
  Base = -> Cut011
  Edges = 1 edges r=2: [Edge1]
FEATURE [Part::Fillet] Fillet012
  Base = -> Fillet011
  Edges = 1 edges r=2.5: [Edge1]
FEATURE [Part::Fillet] Fillet013
  Base = -> Fillet012
  Edges = 1 edges r=2.5: [Edge2]
FEATURE [Part::Box] Box010  label="Cube010"
  AttacherType = Attacher::AttachEngine3D
  Height = 16
  Length = 8
  Placement = pos=(12.7,31.52,28) rot=(0,0,1;0rad)
  Width = 4
FEATURE [Sketcher::SketchObject] Sketch010  label="topSketch004"
  FullyConstrained = true
  sketch-geometry (4):
    g0: LineSegment StartX=16.8446 StartY=31.512 StartZ=0 EndX=16.3251 EndY=34.4666 EndZ=0
    g1: ArcOfCircle CenterX=19 CenterY=19.2524 CenterZ=0 NormalX=0 NormalY=0 NormalZ=1 AngleXU=0 Radius=15.4476 StartAngle=1.74483 EndAngle=2.72717
    g2: ArcOfCircle CenterX=19 CenterY=19.2524 CenterZ=0 NormalX=0 NormalY=0 NormalZ=1 AngleXU=0 Radius=12.4476 StartAngle=1.74483 EndAngle=2.73189
    g3: LineSegment StartX=4.86004 StartY=25.4725 StartZ=0 EndX=7.58253 EndY=24.2107 EndZ=0
  constraints (7):
    c: Block(g0)
    c: Coincident(g1,g0)
    c: Coincident(g2,g0)
    c: Coincident(g3,g1)
    c: Coincident(g3,g2)
    c: Block(g1)
    c: Block(g2)
FEATURE [Part::Cylinder] Cylinder022
  Angle = 360
  AttacherType = Attacher::AttachEngine3D
  Height = 10
  Placement = pos=(0,0,36.15) rot=(0,0,1;0rad)
  Radius = 4
FEATURE [Sketcher::SketchObject] Sketch011  label="topSketch005"
  FullyConstrained = true
  sketch-geometry (4):
    g0: LineSegment StartX=16.8446 StartY=31.512 StartZ=0 EndX=16.3251 EndY=34.4666 EndZ=0
    g1: ArcOfCircle CenterX=19 CenterY=19.2524 CenterZ=0 NormalX=0 NormalY=0 NormalZ=1 AngleXU=0 Radius=15.4476 StartAngle=1.74483 EndAngle=2.72717
    g2: ArcOfCircle CenterX=19 CenterY=19.2524 CenterZ=0 NormalX=0 NormalY=0 NormalZ=1 AngleXU=0 Radius=12.4476 StartAngle=1.74483 EndAngle=2.73189
    g3: LineSegment StartX=4.86004 StartY=25.4725 StartZ=0 EndX=7.58253 EndY=24.2107 EndZ=0
  constraints (7):
    c: Block(g0)
    c: Coincident(g1,g0)
    c: Coincident(g2,g0)
    c: Coincident(g3,g1)
    c: Coincident(g3,g2)
    c: Block(g1)
    c: Block(g2)
FEATURE [Part::Extrusion] Extrude010
  Base = -> Sketch011
  Dir = (0,0,1)
  DirMode = 2
  FaceMakerClass = Part::FaceMakerBullseye
  LengthFwd = 10.6
  LengthRev = 0
  Placement = pos=(0,0,31) rot=(0,0,1;0rad)
  Solid = true
  Symmetric = false
FEATURE [Part::Cylinder] Cylinder023
  Angle = 360
  AttacherType = Attacher::AttachEngine3D
  Height = 20
  Placement = pos=(0,0,36.15) rot=(0,0,1;0rad)
  Radius = 8.2
FEATURE [Part::MultiFuse] Fusion039  label="removeToCreteHoleForPlugHousing008"
  Placement = pos=(-42,19,36) rot=(0,1,0;1.5708rad)
  Shapes = -> [Cylinder023,Cylinder022]
FEATURE [Part::Cut] Cut012
  Base = -> Extrude010
  Placement = pos=(0,0,-0.3) rot=(0,0,1;0rad)
  Tool = -> Fusion039
FEATURE [Part::Cut] Cut013
  Base = -> Box010
  Tool = -> Cut012
FEATURE [Part::Fillet] Fillet014
  Base = -> Cut013
  Edges = 1 edges r=0.7: [Edge13]
FEATURE [Part::Fillet] Fillet015
  Base = -> Fillet014
  Edges = 1 edges r=0.7: [Edge13]
FEATURE [Part::Fillet] Fillet016
  Base = -> Fillet015
  Edges = 1 edges r=0.7: [Edge16]
FEATURE [Part::Fillet] Fillet017
  Base = -> Fillet016
  Edges = 1 edges r=0.7: [Edge11]
FEATURE [Part::Fillet] Fillet018
  Base = -> Fillet017
  Edges = 1 edges r=0.7: [Edge10]
FEATURE [Part::Fillet] Fillet019
  Base = -> Fillet018
  Edges = 1 edges r=1.2: [Edge5]
FEATURE [Part::Fillet] Fillet020
  Base = -> Fillet019
  Edges = 1 edges r=1.2: [Edge12]
FEATURE [Part::Fillet] Fillet021
  Base = -> Fillet020
  Edges = 1 edges r=2: [Edge1]
  Placement = pos=(0.3,0,0) rot=(0,0,1;0rad)
FEATURE [Part::MultiFuse] Fusion040  label="top005"
  Shapes = -> [Cut008,Fillet021]
FEATURE [Part::MultiFuse] Fusion041  label="wireHolder"
  Shapes = -> [Fusion033,Fillet013]
FEATURE [Part::MultiFuse] Fusion042
  Shapes = -> [Fillet007,Fusion041]
FEATURE [Part::MultiFuse] Fusion043  label="wireHolder001"
  Shapes = -> [Fusion042,Fillet010]
FEATURE [Part::MultiFuse] Fusion044  label="wireHolder002"
  Shapes = -> [Fillet006,Fusion037,Fusion043]
FEATURE [Part::Feature] Face026
  shape: bbox 11 x 6 x 2e-07 mm, 1 faces, 0 solids (baked)
FEATURE [Part::Revolution] Revolve026
  Angle = 360
  Axis = (0,1,0)
  Base = (0,0,0)
  FaceMakerClass = Part::FaceMakerBullseye
  Placement = pos=(30.3,-1,19.7) rot=(0,0,1;0rad)
  Solid = false
  Source = -> Face026
  Symmetric = false
FEATURE [Sketcher::SketchObject] Sketch013  label="topSketch006"
  FullyConstrained = true
  sketch-geometry (13):
    g0: LineSegment StartX=117 StartY=19 StartZ=0 EndX=117 EndY=38 EndZ=0
    g1: ArcOfCircle CenterX=98 CenterY=19 CenterZ=0 NormalX=0 NormalY=0 NormalZ=1 AngleXU=0 Radius=19 StartAngle=5.7297 EndAngle=6.28319
    g2: LineSegment StartX=0 StartY=3 StartZ=0 EndX=0 EndY=19 EndZ=0
    g3: LineSegment StartX=19 StartY=38 StartZ=0 EndX=117 EndY=38 EndZ=0
    g4: ArcOfCircle CenterX=19 CenterY=19 CenterZ=0 NormalX=0 NormalY=0 NormalZ=1 AngleXU=0 Radius=19 StartAngle=1.5708 EndAngle=3.14159
    g5: ArcOfCircle CenterX=19 CenterY=19 CenterZ=0 NormalX=0 NormalY=0 NormalZ=1 AngleXU=0 Radius=16 StartAngle=1.5708 EndAngle=3.14159
    g6: ArcOfCircle CenterX=98 CenterY=19 CenterZ=0 NormalX=0 NormalY=0 NormalZ=1 AngleXU=0 Radius=16 StartAngle=5.60905 EndAngle=6.28319
    g7: LineSegment StartX=114 StartY=19 StartZ=0 EndX=114 EndY=35 EndZ=0
    g8: LineSegment StartX=110.5 StartY=9.01251 StartZ=0 EndX=114.163 EndY=9.01251 EndZ=0
    g9: LineSegment StartX=114 StartY=35 StartZ=0 EndX=19 EndY=35 EndZ=0
    g10: LineSegment StartX=0 StartY=3 StartZ=0 EndX=0 EndY=0 EndZ=0
    g11: LineSegment StartX=3 StartY=0 StartZ=0 EndX=0 EndY=0 EndZ=0
    g12: LineSegment StartX=3 StartY=19 StartZ=0 EndX=3 EndY=0 EndZ=0
  constraints (33):
    c: Vertical(g0)
    c: Distance(g0) = 19
    c: Block(g0)
    c: Coincident(g1,g0)
    c: Block(g1)
    c: Vertical(g2)
    c: Block(g2)
    c: Coincident(g3,g0)
    c: Horizontal(g3)
    c: Distance(g3) = 98
    c: Coincident(g4,g3)
    c: Coincident(g4,g2)
    c: Block(g4)
    c: Coincident(g5,g4)
    c: Coincident(g6,g1)
    c: Block(g6)
    c: Block(g5)
    c: Coincident(g7,g6)
    c: Vertical(g7)
    c: Coincident(g8,g6)
    c: Coincident(g8,g1)
    c: Coincident(g9,g7)
    c: Coincident(g9,g5)
    c: Horizontal(g9)
    c: Tangent(g9,g5)
    c: Coincident(g10,g2)
    c: Distance(g10) = 3
    c: Vertical(g10)
    c: Coincident(g11,g10)
    c: Horizontal(g11)
    c: Coincident(g12,g5)
    c: Coincident(g12,g11)
    c: Vertical(g12)
FEATURE [Part::Extrusion] Extrude011  label="top006"
  Base = -> Sketch013
  Dir = (0,0,1)
  DirMode = 2
  FaceMakerClass = Part::FaceMakerBullseye
  LengthFwd = 72
  LengthRev = 0
  Solid = true
  Symmetric = false
FEATURE [Sketcher::SketchObject] Sketch014
  FullyConstrained = true
  MapMode = 3
  Placement = pos=(0,0,0) rot=(1,0,0;1.5708rad)
  Support = -> [Extrude011]
  sketch-geometry (8):
    g0: Circle CenterX=80.351 CenterY=-67.6202 CenterZ=0 NormalX=0 NormalY=0 NormalZ=1 AngleXU=0 Radius=2
    g1: Circle CenterX=80.351 CenterY=-67.6202 CenterZ=0 NormalX=0 NormalY=0 NormalZ=1 AngleXU=0 Radius=3
    g2: Circle CenterX=80.351 CenterY=-4.92017 CenterZ=0 NormalX=0 NormalY=0 NormalZ=1 AngleXU=0 Radius=2
    g3: Circle CenterX=80.351 CenterY=-4.92017 CenterZ=0 NormalX=0 NormalY=0 NormalZ=1 AngleXU=0 Radius=3
    g4: Circle CenterX=23.851 CenterY=-4.92017 CenterZ=0 NormalX=0 NormalY=0 NormalZ=1 AngleXU=0 Radius=2
    g5: Circle CenterX=23.851 CenterY=-4.92017 CenterZ=0 NormalX=0 NormalY=0 NormalZ=1 AngleXU=0 Radius=3
    g6: Circle CenterX=23.851 CenterY=-67.6202 CenterZ=0 NormalX=0 NormalY=0 NormalZ=1 AngleXU=0 Radius=2
    g7: Circle CenterX=23.851 CenterY=-67.6202 CenterZ=0 NormalX=0 NormalY=0 NormalZ=1 AngleXU=0 Radius=3
  constraints (8):
    c: Block(g3)
    c: Block(g2)
    c: Block(g1)
    c: Block(g0)
    c: Block(g6)
    c: Block(g7)
    c: Block(g4)
    c: Block(g5)
FEATURE [Part::Feature] Face027
  shape: bbox 11 x 6 x 2e-07 mm, 1 faces, 0 solids (baked)
FEATURE [Part::Revolution] Revolve027
  Angle = 360
  Axis = (0,1,0)
  Base = (0,0,0)
  FaceMakerClass = Part::FaceMakerBullseye
  Placement = pos=(30.3,-1,51.7) rot=(0,0,1;0rad)
  Solid = false
  Source = -> Face027
  Symmetric = false
FEATURE [Part::Feature] Face028
  shape: bbox 11 x 6 x 2e-07 mm, 1 faces, 0 solids (baked)
FEATURE [Part::Revolution] Revolve028
  Angle = 360
  Axis = (0,1,0)
  Base = (0,0,0)
  FaceMakerClass = Part::FaceMakerBullseye
  Placement = pos=(62.3,-1,19.7) rot=(0,0,1;0rad)
  Solid = false
  Source = -> Face028
  Symmetric = false
FEATURE [Part::Feature] Face029
  shape: bbox 11 x 6 x 2e-07 mm, 1 faces, 0 solids (baked)
FEATURE [Part::Revolution] Revolve029
  Angle = 360
  Axis = (0,1,0)
  Base = (0,0,0)
  FaceMakerClass = Part::FaceMakerBullseye
  Placement = pos=(62.3,-1,51.7) rot=(0,0,1;0rad)
  Solid = false
  Source = -> Face029
  Symmetric = false
FEATURE [Part::Feature] Wire
  shape: bbox 11 x 5.2 x 2e-07 mm, 0 faces, 0 solids (baked)
FEATURE [Part::Revolution] Revolve030
  Angle = 360
  Axis = (0,1,0)
  Base = (0,0,0)
  FaceMakerClass = Part::FaceMakerBullseye
  Placement = pos=(30.3,38,19.7) rot=(0,0,1;0rad)
  Solid = true
  Source = -> Wire
  Symmetric = false
FEATURE [Part::Feature] Wire001
  shape: bbox 11 x 5.2 x 2e-07 mm, 0 faces, 0 solids (baked)
FEATURE [Part::Revolution] Revolve031
  Angle = 360
  Axis = (0,1,0)
  Base = (0,0,0)
  FaceMakerClass = Part::FaceMakerBullseye
  Placement = pos=(30.3,38,51.7) rot=(0,0,1;0rad)
  Solid = true
  Source = -> Wire001
  Symmetric = false
FEATURE [Part::Feature] Wire002
  shape: bbox 11 x 5.2 x 2e-07 mm, 0 faces, 0 solids (baked)
FEATURE [Part::Revolution] Revolve032
  Angle = 360
  Axis = (0,1,0)
  Base = (0,0,0)
  FaceMakerClass = Part::FaceMakerBullseye
  Placement = pos=(62.3,38,51.7) rot=(0,0,1;0rad)
  Solid = true
  Source = -> Wire002
  Symmetric = false
FEATURE [Part::Feature] Wire003
  shape: bbox 11 x 5.2 x 2e-07 mm, 0 faces, 0 solids (baked)
FEATURE [Part::Revolution] Revolve033
  Angle = 360
  Axis = (0,1,0)
  Base = (0,0,0)
  FaceMakerClass = Part::FaceMakerBullseye
  Placement = pos=(62.3,38,19.7) rot=(0,0,1;0rad)
  Solid = true
  Source = -> Wire003
  Symmetric = false
FEATURE [Part::MultiFuse] Fusion045  label="altRandScrewHousing"
  Shapes = -> [Revolve029,Revolve027,Revolve028,Revolve026]
FEATURE [Part::MultiFuse] Fusion046  label="fanScrewHousing"
  Shapes = -> [Revolve033,Revolve032,Revolve031,Revolve030]
FEATURE [Sketcher::SketchObject] Sketch015
  FullyConstrained = true
  sketch-geometry (17):
    g0: Circle CenterX=-3.5 CenterY=23.5 CenterZ=0 NormalX=0 NormalY=0 NormalZ=1 AngleXU=0 Radius=1
    g1: Circle CenterX=-1 CenterY=15.25 CenterZ=0 NormalX=0 NormalY=0 NormalZ=1 AngleXU=0 Radius=1
    g2: Circle CenterX=-3.5 CenterY=7 CenterZ=0 NormalX=0 NormalY=0 NormalZ=1 AngleXU=0 Radius=1
    g3: BSplineCurve PolesCount=3 KnotsCount=2 Degree=2 IsPeriodic=0
    g4: GeomPoint X=-3.5 Y=23.5 Z=0
    g5: GeomPoint X=-3.5 Y=7 Z=0
    g6: Circle CenterX=-4.8 CenterY=30.5 CenterZ=0 NormalX=0 NormalY=0 NormalZ=1 AngleXU=0 Radius=1
    g7: Circle CenterX=-3.5 CenterY=30.5 CenterZ=0 NormalX=0 NormalY=0 NormalZ=1 AngleXU=0 Radius=1
    g8: Circle CenterX=-3.5 CenterY=29.2 CenterZ=0 NormalX=0 NormalY=0 NormalZ=1 AngleXU=0 Radius=1
    g9: BSplineCurve PolesCount=3 KnotsCount=2 Degree=2 IsPeriodic=0
    g10: GeomPoint X=-4.8 Y=30.5 Z=0
    g11: GeomPoint X=-3.5 Y=29.2 Z=0
    g12: LineSegment StartX=-3.5 StartY=29.2 StartZ=0 EndX=-3.5 EndY=23.5 EndZ=0
    g13: LineSegment StartX=-4.8 StartY=30.5 StartZ=0 EndX=0 EndY=30.5 EndZ=0
    g14: LineSegment StartX=-3.5 StartY=0.3 StartZ=0 EndX=0 EndY=0.3 EndZ=0
    g15: LineSegment StartX=-3.5 StartY=0.3 StartZ=0 EndX=-3.5 EndY=7 EndZ=0
    g16: LineSegment StartX=0 StartY=0.3 StartZ=0 EndX=0 EndY=30.5 EndZ=0
  constraints (33):
    c: Weight(g0) = 1
    c: Equal(g0,g1)
    c: Equal(g0,g2)
    c: InternalAlignment(g0,g3)
    c: InternalAlignment(g1,g3)
    c: InternalAlignment(g2,g3)
    c: InternalAlignment(g4,g3)
    c: InternalAlignment(g5,g3)
    c: Block(g3)
    c: Weight(g6) = 1
    c: Equal(g6,g7)
    c: Equal(g6,g8)
    c: InternalAlignment(g6,g9)
    c: InternalAlignment(g7,g9)
    c: InternalAlignment(g8,g9)
    c: InternalAlignment(g10,g9)
    c: InternalAlignment(g11,g9)
    c: Block(g9)
    c: Coincident(g12,g9)
    c: Coincident(g12,g3)
    c: Vertical(g12)
    c: Coincident(g13,g9)
    c: Horizontal(g13)
    c: Distance(g13) = 4.8
    c: Horizontal(g14)
    c: Block(g14)
    c: Coincident(g15,g14)
    c: Coincident(g15,g3)
    c: Vertical(g15)
    c: Coincident(g16,g14)
    c: Coincident(g16,g13)
    c: Vertical(g16)
    c: Tangent(g16,g1)
FEATURE [Sketcher::SketchObject] Sketch016
  FullyConstrained = true
  sketch-geometry (16):
    g0: Circle CenterX=-3.5 CenterY=23.5 CenterZ=0 NormalX=0 NormalY=0 NormalZ=1 AngleXU=0 Radius=1
    g1: Circle CenterX=-1 CenterY=15.25 CenterZ=0 NormalX=0 NormalY=0 NormalZ=1 AngleXU=0 Radius=1
    g2: Circle CenterX=-3.5 CenterY=7 CenterZ=0 NormalX=0 NormalY=0 NormalZ=1 AngleXU=0 Radius=1
    g3: BSplineCurve PolesCount=3 KnotsCount=2 Degree=2 IsPeriodic=0
    g4: GeomPoint X=-3.5 Y=23.5 Z=0
    g5: GeomPoint X=-3.5 Y=7 Z=0
    g6: LineSegment StartX=-3.5 StartY=28.2 StartZ=0 EndX=-3.5 EndY=23.5 EndZ=0
    g7: LineSegment StartX=0 StartY=29.5 StartZ=0 EndX=0 EndY=30 EndZ=0
    g8: LineSegment StartX=-3.5 StartY=28.2 StartZ=0 EndX=-3.5 EndY=30 EndZ=0
    g9: LineSegment StartX=0 StartY=30 StartZ=0 EndX=0 EndY=30.5 EndZ=0
    g10: LineSegment StartX=0 StartY=30.5 StartZ=0 EndX=-3.5 EndY=30.5 EndZ=0
    g11: LineSegment StartX=-3.5 StartY=30.5 StartZ=0 EndX=-3.5 EndY=30 EndZ=0
    g12: LineSegment StartX=0 StartY=29.5 StartZ=0 EndX=0 EndY=5 EndZ=0
    g13: LineSegment StartX=-3.5 StartY=0.3 StartZ=0 EndX=-3.5 EndY=7 EndZ=0
    g14: LineSegment StartX=-3.5 StartY=0.3 StartZ=0 EndX=0 EndY=0.3 EndZ=0
    g15: LineSegment StartX=0 StartY=5 StartZ=0 EndX=0 EndY=0.3 EndZ=0
  constraints (39):
    c: Weight(g0) = 1
    c: Equal(g0,g1)
    c: Equal(g0,g2)
    c: InternalAlignment(g0,g3)
    c: InternalAlignment(g1,g3)
    c: InternalAlignment(g2,g3)
    c: InternalAlignment(g4,g3)
    c: InternalAlignment(g5,g3)
    c: Block(g3)
    c: Coincident(g6,g3)
    c: Vertical(g6)
    c: Vertical(g7)
    c: Distance(g7) = 0.5
    c: Coincident(g8,g6)
    c: Vertical(g8)
    c: Block(g6)
    c: Block(g7)
    c: Vertical(g9)
    c: Equal(g7,g9) = 0.5
    c: Block(g9)
    c: Coincident(g9,g7)
    c: Horizontal(g10)
    c: Coincident(g10,g9)
    c: Coincident(g11,g10)
    c: Coincident(g11,g8)
    c: Vertical(g11)
    c: Block(g11)
    c: Coincident(g12,g7)
    c: Vertical(g12)
    c: Coincident(g13,g3)
    c: Vertical(g13)
    c: Distance(g13) = 6.7
    c: Coincident(g14,g13)
    c: Horizontal(g14)
    c: Block(g14)
    c: Coincident(g15,g12)
    c: Coincident(g15,g14)
    c: Vertical(g15)
    c: Block(g15)
FEATURE [Sketcher::SketchObject] Sketch017
  FullyConstrained = true
  sketch-geometry (11):
    g0: LineSegment StartX=-3.5 StartY=1e-16 StartZ=0 EndX=-1.6 EndY=1e-16 EndZ=0
    g1: LineSegment StartX=-1.6 StartY=1e-16 StartZ=0 EndX=-1.6 EndY=1.5 EndZ=0
    g2: LineSegment StartX=-3.5 StartY=1.5 StartZ=0 EndX=-1.6 EndY=1.5 EndZ=0
    g3: LineSegment StartX=-3.5 StartY=1e-16 StartZ=0 EndX=-4.8 EndY=1e-16 EndZ=0
    g4: Circle CenterX=-3.5 CenterY=1.3 CenterZ=0 NormalX=0 NormalY=0 NormalZ=1 AngleXU=0 Radius=1
    g5: Circle CenterX=-3.5 CenterY=1e-16 CenterZ=0 NormalX=0 NormalY=0 NormalZ=1 AngleXU=0 Radius=1
    g6: Circle CenterX=-4.8 CenterY=1e-16 CenterZ=0 NormalX=0 NormalY=0 NormalZ=1 AngleXU=0 Radius=1
    g7: BSplineCurve PolesCount=3 KnotsCount=2 Degree=2 IsPeriodic=0
    g8: GeomPoint X=-3.5 Y=1.3 Z=0
    g9: GeomPoint X=-4.8 Y=1e-16 Z=0
    g10: LineSegment StartX=-3.5 StartY=1.3 StartZ=0 EndX=-3.5 EndY=1.5 EndZ=0
  constraints (24):
    c: Horizontal(g0)
    c: Distance(g0) = 1.9
    c: Block(g0)
    c: Coincident(g1,g0)
    c: Vertical(g1)
    c: Coincident(g2,g1)
    c: Horizontal(g2)
    c: Coincident(g3,g0)
    c: Horizontal(g3)
    c: Distance(g3) = 1.3
    c: Weight(g4) = 1
    c: Equal(g4,g5)
    c: Coincident(g5,g0)
    c: Equal(g4,g6)
    c: Coincident(g7,g3)
    c: InternalAlignment(g4,g7)
    c: InternalAlignment(g5,g7)
    c: InternalAlignment(g6,g7)
    c: InternalAlignment(g8,g7)
    c: InternalAlignment(g9,g7)
    c: Coincident(g10,g7)
    c: Coincident(g10,g2)
    c: Vertical(g10)
    c: Block(g10)
FEATURE [Part::Feature] Face035
  shape: bbox 3.2 x 1.5 x 2e-07 mm, 1 faces, 0 solids (baked)
FEATURE [Part::Revolution] Revolve039  label="backCaseScrewRetainer"
  Angle = 360
  Axis = (0,1,0)
  Base = (0,0,0)
  FaceMakerClass = Part::FaceMakerBullseye
  Placement = pos=(12.5,3,62) rot=(0,0,1;0rad)
  Solid = false
  Source = -> Face035
  Symmetric = false
FEATURE [Part::Feature] Face036
  shape: bbox 3.2 x 1.5 x 2e-07 mm, 1 faces, 0 solids (baked)
FEATURE [Part::Feature] Face039
  shape: bbox 4.8 x 30.2 x 2e-07 mm, 1 faces, 0 solids (baked)
FEATURE [Part::Revolution] Revolve043  label="frontCaseScrewPost002"
  Angle = 360
  Axis = (0,1,0)
  Base = (0,0,0)
  FaceMakerClass = Part::FaceMakerBullseye
  Placement = pos=(89.5,4.5,3.5) rot=(0,0,1;0rad)
  Solid = false
  Source = -> Face039
  Symmetric = false
FEATURE [Part::Feature] Face042
  shape: bbox 4.8 x 30.2 x 2e-07 mm, 1 faces, 0 solids (baked)
FEATURE [Part::Revolution] Revolve046  label="frontCaseScrewPost003"
  Angle = 360
  Axis = (0,1,0)
  Base = (0,0,0)
  FaceMakerClass = Part::FaceMakerBullseye
  Placement = pos=(89.5,4.5,68.5) rot=(0,0,1;0rad)
  Solid = false
  Source = -> Face042
  Symmetric = false
FEATURE [Part::Feature] Face043
  shape: bbox 3.2 x 1.5 x 2e-07 mm, 1 faces, 0 solids (baked)
FEATURE [Part::Revolution] Revolve047  label="frontCaseScrewRetainer002"
  Angle = 360
  Axis = (0,1,0)
  Base = (0,0,0)
  FaceMakerClass = Part::FaceMakerBullseye
  Placement = pos=(89.5,3,68.5) rot=(0,0,1;0rad)
  Solid = false
  Source = -> Face043
  Symmetric = false
FEATURE [Part::Feature] Face044
  shape: bbox 3.2 x 1.5 x 2e-07 mm, 1 faces, 0 solids (baked)
FEATURE [Part::Revolution] Revolve048  label="frontCaseScrewRetainer003"
  Angle = 360
  Axis = (0,1,0)
  Base = (0,0,0)
  FaceMakerClass = Part::FaceMakerBullseye
  Placement = pos=(89.5,3,3.5) rot=(0,0,1;0rad)
  Solid = false
  Source = -> Face044
  Symmetric = false
FEATURE [App::MeasureDistance] Distance002  label="Distance: 1.67 mm"
  Distance = 1.66921
  P1 = (99.2361,4.7524,71.7)
  P2 = (99.2347,6.42161,71.7)
FEATURE [Sketcher::SketchObject] Sketch018
  FullyConstrained = true
  sketch-geometry (7):
    g0: LineSegment StartX=0 StartY=0 StartZ=0 EndX=0 EndY=6 EndZ=0
    g1: Circle CenterX=0 CenterY=0 CenterZ=0 NormalX=0 NormalY=0 NormalZ=1 AngleXU=0 Radius=1
    g2: Circle CenterX=8 CenterY=6 CenterZ=0 NormalX=0 NormalY=0 NormalZ=1 AngleXU=0 Radius=1
    g3: BSplineCurve PolesCount=3 KnotsCount=2 Degree=2 IsPeriodic=0
    g4: GeomPoint X=0 Y=0 Z=0
    g5: GeomPoint X=8 Y=6 Z=0
    g6: LineSegment StartX=0 StartY=6 StartZ=0 EndX=8 EndY=6 EndZ=0
  constraints (14):
    c: Coincident(g0,g-1)
    c: Distance(g0) = 6
    c: Vertical(g0)
    c: Coincident(g3,g0)
    c: Weight(g1) = 1
    c: Equal(g1,g2)
    c: InternalAlignment(g1,g3)
    c: InternalAlignment(g2,g3)
    c: InternalAlignment(g4,g3)
    c: InternalAlignment(g5,g3)
    c: Block(g3)
    c: Coincident(g6,g0)
    c: Coincident(g6,g3)
    c: Horizontal(g6)
FEATURE [Part::Extrusion] Extrude012  label="caseScrewPillarBracket"
  Base = -> Sketch018
  Dir = (0,0,1)
  DirMode = 2
  FaceMakerClass = Part::FaceMakerBullseye
  LengthFwd = 2.4
  LengthRev = 0
  Placement = pos=(15.76,29,8.8) rot=(0,1,0;0rad)
  Solid = true
  Symmetric = false
FEATURE [Sketcher::SketchObject] Sketch019
  FullyConstrained = true
  sketch-geometry (7):
    g0: LineSegment StartX=0 StartY=0 StartZ=0 EndX=0 EndY=6 EndZ=0
    g1: Circle CenterX=0 CenterY=0 CenterZ=0 NormalX=0 NormalY=0 NormalZ=1 AngleXU=0 Radius=1
    g2: Circle CenterX=8 CenterY=6 CenterZ=0 NormalX=0 NormalY=0 NormalZ=1 AngleXU=0 Radius=1
    g3: BSplineCurve PolesCount=3 KnotsCount=2 Degree=2 IsPeriodic=0
    g4: GeomPoint X=0 Y=0 Z=0
    g5: GeomPoint X=8 Y=6 Z=0
    g6: LineSegment StartX=0 StartY=6 StartZ=0 EndX=8 EndY=6 EndZ=0
  constraints (14):
    c: Coincident(g0,g-1)
    c: Distance(g0) = 6
    c: Vertical(g0)
    c: Coincident(g3,g0)
    c: Weight(g1) = 1
    c: Equal(g1,g2)
    c: InternalAlignment(g1,g3)
    c: InternalAlignment(g2,g3)
    c: InternalAlignment(g4,g3)
    c: InternalAlignment(g5,g3)
    c: Block(g3)
    c: Coincident(g6,g0)
    c: Coincident(g6,g3)
    c: Horizontal(g6)
FEATURE [Part::Extrusion] Extrude013  label="caseScrewPillarBracket001"
  Base = -> Sketch019
  Dir = (0,0,1)
  DirMode = 2
  FaceMakerClass = Part::FaceMakerBullseye
  LengthFwd = 2.4
  LengthRev = 0
  Placement = pos=(15.76,29,60.8) rot=(0,0,1;0rad)
  Solid = true
  Symmetric = false
FEATURE [Sketcher::SketchObject] Sketch020
  FullyConstrained = true
  sketch-geometry (7):
    g0: LineSegment StartX=0 StartY=0 StartZ=0 EndX=0 EndY=6 EndZ=0
    g1: Circle CenterX=0 CenterY=0 CenterZ=0 NormalX=0 NormalY=0 NormalZ=1 AngleXU=0 Radius=1
    g2: Circle CenterX=8 CenterY=6 CenterZ=0 NormalX=0 NormalY=0 NormalZ=1 AngleXU=0 Radius=1
    g3: BSplineCurve PolesCount=3 KnotsCount=2 Degree=2 IsPeriodic=0
    g4: GeomPoint X=0 Y=0 Z=0
    g5: GeomPoint X=8 Y=6 Z=0
    g6: LineSegment StartX=0 StartY=6 StartZ=0 EndX=8 EndY=6 EndZ=0
  constraints (14):
    c: Coincident(g0,g-1)
    c: Distance(g0) = 6
    c: Vertical(g0)
    c: Coincident(g3,g0)
    c: Weight(g1) = 1
    c: Equal(g1,g2)
    c: InternalAlignment(g1,g3)
    c: InternalAlignment(g2,g3)
    c: InternalAlignment(g4,g3)
    c: InternalAlignment(g5,g3)
    c: Block(g3)
    c: Coincident(g6,g0)
    c: Coincident(g6,g3)
    c: Horizontal(g6)
FEATURE [Part::Extrusion] Extrude014  label="caseScrewPillarBracket002"
  Base = -> Sketch020
  Dir = (0,0,1)
  DirMode = 2
  FaceMakerClass = Part::FaceMakerBullseye
  LengthFwd = 2.4
  LengthRev = 0
  Placement = pos=(13.7,29,13.26) rot=(0,1,0;-1.5708rad)
  Solid = true
  Symmetric = false
FEATURE [Sketcher::SketchObject] Sketch021
  FullyConstrained = true
  sketch-geometry (7):
    g0: LineSegment StartX=0 StartY=0 StartZ=0 EndX=0 EndY=6 EndZ=0
    g1: Circle CenterX=0 CenterY=0 CenterZ=0 NormalX=0 NormalY=0 NormalZ=1 AngleXU=0 Radius=1
    g2: Circle CenterX=8 CenterY=6 CenterZ=0 NormalX=0 NormalY=0 NormalZ=1 AngleXU=0 Radius=1
    g3: BSplineCurve PolesCount=3 KnotsCount=2 Degree=2 IsPeriodic=0
    g4: GeomPoint X=0 Y=0 Z=0
    g5: GeomPoint X=8 Y=6 Z=0
    g6: LineSegment StartX=0 StartY=6 StartZ=0 EndX=8 EndY=6 EndZ=0
  constraints (14):
    c: Coincident(g0,g-1)
    c: Distance(g0) = 6
    c: Vertical(g0)
    c: Coincident(g3,g0)
    c: Weight(g1) = 1
    c: Equal(g1,g2)
    c: InternalAlignment(g1,g3)
    c: InternalAlignment(g2,g3)
    c: InternalAlignment(g4,g3)
    c: InternalAlignment(g5,g3)
    c: Block(g3)
    c: Coincident(g6,g0)
    c: Coincident(g6,g3)
    c: Horizontal(g6)
FEATURE [Part::Extrusion] Extrude015  label="caseScrewPillarBracket003"
  Base = -> Sketch021
  Dir = (0,0,1)
  DirMode = 2
  FaceMakerClass = Part::FaceMakerBullseye
  LengthFwd = 2.4
  LengthRev = 0
  Placement = pos=(11.3,29,58.74) rot=(0,1,0;1.5708rad)
  Solid = true
  Symmetric = false
FEATURE [Sketcher::SketchObject] Sketch022
  FullyConstrained = true
  sketch-geometry (7):
    g0: LineSegment StartX=0 StartY=0 StartZ=0 EndX=0 EndY=6 EndZ=0
    g1: Circle CenterX=0 CenterY=0 CenterZ=0 NormalX=0 NormalY=0 NormalZ=1 AngleXU=0 Radius=1
    g2: Circle CenterX=8 CenterY=6 CenterZ=0 NormalX=0 NormalY=0 NormalZ=1 AngleXU=0 Radius=1
    g3: BSplineCurve PolesCount=3 KnotsCount=2 Degree=2 IsPeriodic=0
    g4: GeomPoint X=0 Y=0 Z=0
    g5: GeomPoint X=8 Y=6 Z=0
    g6: LineSegment StartX=0 StartY=6 StartZ=0 EndX=8 EndY=6 EndZ=0
  constraints (14):
    c: Coincident(g0,g-1)
    c: Distance(g0) = 6
    c: Vertical(g0)
    c: Coincident(g3,g0)
    c: Weight(g1) = 1
    c: Equal(g1,g2)
    c: InternalAlignment(g1,g3)
    c: InternalAlignment(g2,g3)
    c: InternalAlignment(g4,g3)
    c: InternalAlignment(g5,g3)
    c: Block(g3)
    c: Coincident(g6,g0)
    c: Coincident(g6,g3)
    c: Horizontal(g6)
FEATURE [Part::Extrusion] Extrude016  label="caseScrewPillarBracket004"
  Base = -> Sketch022
  Dir = (0,0,1)
  DirMode = 2
  FaceMakerClass = Part::FaceMakerBullseye
  LengthFwd = 2.4
  LengthRev = 0
  Placement = pos=(88.3,29,65.23) rot=(0,1,0;1.5708rad)
  Solid = true
  Symmetric = false
FEATURE [Sketcher::SketchObject] Sketch023
  FullyConstrained = true
  sketch-geometry (7):
    g0: LineSegment StartX=0 StartY=0 StartZ=0 EndX=0 EndY=6 EndZ=0
    g1: Circle CenterX=0 CenterY=0 CenterZ=0 NormalX=0 NormalY=0 NormalZ=1 AngleXU=0 Radius=1
    g2: Circle CenterX=8 CenterY=6 CenterZ=0 NormalX=0 NormalY=0 NormalZ=1 AngleXU=0 Radius=1
    g3: BSplineCurve PolesCount=3 KnotsCount=2 Degree=2 IsPeriodic=0
    g4: GeomPoint X=0 Y=0 Z=0
    g5: GeomPoint X=8 Y=6 Z=0
    g6: LineSegment StartX=0 StartY=6 StartZ=0 EndX=8 EndY=6 EndZ=0
  constraints (14):
    c: Coincident(g0,g-1)
    c: Distance(g0) = 6
    c: Vertical(g0)
    c: Coincident(g3,g0)
    c: Weight(g1) = 1
    c: Equal(g1,g2)
    c: InternalAlignment(g1,g3)
    c: InternalAlignment(g2,g3)
    c: InternalAlignment(g4,g3)
    c: InternalAlignment(g5,g3)
    c: Block(g3)
    c: Coincident(g6,g0)
    c: Coincident(g6,g3)
    c: Horizontal(g6)
FEATURE [Part::Extrusion] Extrude017  label="caseScrewPillarBracket005"
  Base = -> Sketch023
  Dir = (0,0,1)
  DirMode = 2
  FaceMakerClass = Part::FaceMakerBullseye
  LengthFwd = 2.4
  LengthRev = 0
  Placement = pos=(90.7,29,6.77) rot=(0,-1,0;1.5708rad)
  Solid = true
  Symmetric = false
FEATURE [Sketcher::SketchObject] Sketch024
  FullyConstrained = true
  sketch-geometry (7):
    g0: LineSegment StartX=0 StartY=0 StartZ=0 EndX=0 EndY=6 EndZ=0
    g1: Circle CenterX=0 CenterY=0 CenterZ=0 NormalX=0 NormalY=0 NormalZ=1 AngleXU=0 Radius=1
    g2: Circle CenterX=8 CenterY=6 CenterZ=0 NormalX=0 NormalY=0 NormalZ=1 AngleXU=0 Radius=1
    g3: BSplineCurve PolesCount=3 KnotsCount=2 Degree=2 IsPeriodic=0
    g4: GeomPoint X=0 Y=0 Z=0
    g5: GeomPoint X=8 Y=6 Z=0
    g6: LineSegment StartX=0 StartY=6 StartZ=0 EndX=8 EndY=6 EndZ=0
  constraints (14):
    c: Coincident(g0,g-1)
    c: Distance(g0) = 6
    c: Vertical(g0)
    c: Coincident(g3,g0)
    c: Weight(g1) = 1
    c: Equal(g1,g2)
    c: InternalAlignment(g1,g3)
    c: InternalAlignment(g2,g3)
    c: InternalAlignment(g4,g3)
    c: InternalAlignment(g5,g3)
    c: Block(g3)
    c: Coincident(g6,g0)
    c: Coincident(g6,g3)
    c: Horizontal(g6)
FEATURE [Part::Extrusion] Extrude018  label="caseScrewPillarBracket006"
  Base = -> Sketch024
  Dir = (0,0,1)
  DirMode = 2
  FaceMakerClass = Part::FaceMakerBullseye
  LengthFwd = 2.4
  LengthRev = 0
  Placement = pos=(103.7,29,6.77) rot=(0,-1,0;1.5708rad)
  Solid = true
  Symmetric = false
FEATURE [Sketcher::SketchObject] Sketch025
  FullyConstrained = true
  sketch-geometry (7):
    g0: LineSegment StartX=0 StartY=0 StartZ=0 EndX=0 EndY=6 EndZ=0
    g1: Circle CenterX=0 CenterY=0 CenterZ=0 NormalX=0 NormalY=0 NormalZ=1 AngleXU=0 Radius=1
    g2: Circle CenterX=8 CenterY=6 CenterZ=0 NormalX=0 NormalY=0 NormalZ=1 AngleXU=0 Radius=1
    g3: BSplineCurve PolesCount=3 KnotsCount=2 Degree=2 IsPeriodic=0
    g4: GeomPoint X=0 Y=0 Z=0
    g5: GeomPoint X=8 Y=6 Z=0
    g6: LineSegment StartX=0 StartY=6 StartZ=0 EndX=8 EndY=6 EndZ=0
  constraints (14):
    c: Coincident(g0,g-1)
    c: Distance(g0) = 6
    c: Vertical(g0)
    c: Coincident(g3,g0)
    c: Weight(g1) = 1
    c: Equal(g1,g2)
    c: InternalAlignment(g1,g3)
    c: InternalAlignment(g2,g3)
    c: InternalAlignment(g4,g3)
    c: InternalAlignment(g5,g3)
    c: Block(g3)
    c: Coincident(g6,g0)
    c: Coincident(g6,g3)
    c: Horizontal(g6)
FEATURE [Part::Extrusion] Extrude019  label="caseScrewPillarBracket007"
  Base = -> Sketch025
  Dir = (0,0,1)
  DirMode = 2
  FaceMakerClass = Part::FaceMakerBullseye
  LengthFwd = 2.4
  LengthRev = 0
  Placement = pos=(101.3,29,65.23) rot=(0,1,0;1.5708rad)
  Solid = true
  Symmetric = false
FEATURE [Part::Box] Box011  label="frontCaseScrewPillarBracket"
  AttacherType = Attacher::AttachEngine3D
  Height = 2.4
  Length = 16
  Placement = pos=(87,28,2.3) rot=(0,0,1;0rad)
  Width = 7
FEATURE [Part::Box] Box012  label="frontCaseScrewPillarBracket001"
  AttacherType = Attacher::AttachEngine3D
  Height = 2.4
  Length = 16
  Placement = pos=(87,28,67.3) rot=(0,0,1;0rad)
  Width = 7
FEATURE [Sketcher::SketchObject] Sketch026
  FullyConstrained = true
  sketch-geometry (17):
    g0: Circle CenterX=-3.5 CenterY=23.5 CenterZ=0 NormalX=0 NormalY=0 NormalZ=1 AngleXU=0 Radius=1
    g1: Circle CenterX=-1 CenterY=15.25 CenterZ=0 NormalX=0 NormalY=0 NormalZ=1 AngleXU=0 Radius=1
    g2: Circle CenterX=-3.5 CenterY=7 CenterZ=0 NormalX=0 NormalY=0 NormalZ=1 AngleXU=0 Radius=1
    g3: BSplineCurve PolesCount=3 KnotsCount=2 Degree=2 IsPeriodic=0
    g4: GeomPoint X=-3.5 Y=23.5 Z=0
    g5: GeomPoint X=-3.5 Y=7 Z=0
    g6: Circle CenterX=-4.8 CenterY=30.5 CenterZ=0 NormalX=0 NormalY=0 NormalZ=1 AngleXU=0 Radius=1
    g7: Circle CenterX=-3.5 CenterY=30.5 CenterZ=0 NormalX=0 NormalY=0 NormalZ=1 AngleXU=0 Radius=1
    g8: Circle CenterX=-3.5 CenterY=29.2 CenterZ=0 NormalX=0 NormalY=0 NormalZ=1 AngleXU=0 Radius=1
    g9: BSplineCurve PolesCount=3 KnotsCount=2 Degree=2 IsPeriodic=0
    g10: GeomPoint X=-4.8 Y=30.5 Z=0
    g11: GeomPoint X=-3.5 Y=29.2 Z=0
    g12: LineSegment StartX=-3.5 StartY=29.2 StartZ=0 EndX=-3.5 EndY=23.5 EndZ=0
    g13: LineSegment StartX=-4.8 StartY=30.5 StartZ=0 EndX=0 EndY=30.5 EndZ=0
    g14: LineSegment StartX=-3.5 StartY=5 StartZ=0 EndX=-3.5 EndY=7 EndZ=0
    g15: LineSegment StartX=0 StartY=5 StartZ=0 EndX=0 EndY=30.5 EndZ=0
    g16: LineSegment StartX=-3.5 StartY=5 StartZ=0 EndX=0 EndY=5 EndZ=0
  constraints (33):
    c: Weight(g0) = 1
    c: Equal(g0,g1)
    c: Equal(g0,g2)
    c: InternalAlignment(g0,g3)
    c: InternalAlignment(g1,g3)
    c: InternalAlignment(g2,g3)
    c: InternalAlignment(g4,g3)
    c: InternalAlignment(g5,g3)
    c: Block(g3)
    c: Weight(g6) = 1
    c: Equal(g6,g7)
    c: Equal(g6,g8)
    c: InternalAlignment(g6,g9)
    c: InternalAlignment(g7,g9)
    c: InternalAlignment(g8,g9)
    c: InternalAlignment(g10,g9)
    c: InternalAlignment(g11,g9)
    c: Block(g9)
    c: Coincident(g12,g9)
    c: Coincident(g12,g3)
    c: Vertical(g12)
    c: Coincident(g13,g9)
    c: Horizontal(g13)
    c: Distance(g13) = 4.8
    c: Coincident(g14,g3)
    c: Vertical(g14)
    c: Coincident(g15,g13)
    c: Vertical(g15)
    c: Tangent(g15,g1)
    c: Distance(g14) = 2
    c: Coincident(g16,g14)
    c: Horizontal(g16)
    c: Coincident(g15,g16)
FEATURE [Part::Feature] Face050
  shape: bbox 4.8 x 25.5 x 2e-07 mm, 1 faces, 0 solids (baked)
FEATURE [Part::Revolution] Revolve054  label="moreFrontCaseScrewPost001"
  Angle = 360
  Axis = (0,1,0)
  Base = (0,0,0)
  FaceMakerClass = Part::FaceMakerBullseye
  Placement = pos=(102.5,4.5,3.5) rot=(0,0,1;0rad)
  Solid = false
  Source = -> Face050
  Symmetric = false
FEATURE [Part::Feature] Face051
  shape: bbox 4.8 x 25.5 x 2e-07 mm, 1 faces, 0 solids (baked)
FEATURE [Part::Revolution] Revolve055  label="moreFrontCaseScrewPost002"
  Angle = 360
  Axis = (0,1,0)
  Base = (0,0,0)
  FaceMakerClass = Part::FaceMakerBullseye
  Placement = pos=(102.5,4.5,68.5) rot=(0,0,1;0rad)
  Solid = false
  Source = -> Face051
  Symmetric = false
FEATURE [Sketcher::SketchObject] Sketch027
  FullyConstrained = true
  sketch-geometry (10):
    g0: LineSegment StartX=-1.6 StartY=4.7 StartZ=0 EndX=-1.6 EndY=1.7 EndZ=0
    g1: LineSegment StartX=-3.5 StartY=4.7 StartZ=0 EndX=-1.6 EndY=4.7 EndZ=0
    g2: LineSegment StartX=-1.6 StartY=1.7 StartZ=0 EndX=-1.6 EndY=1.5 EndZ=0
    g3: LineSegment StartX=-1.6 StartY=1.5 StartZ=0 EndX=-5.2 EndY=1.5 EndZ=0
    g4: Circle CenterX=-3.5 CenterY=4.7 CenterZ=0 NormalX=0 NormalY=0 NormalZ=1 AngleXU=0 Radius=1
    g5: Circle CenterX=-3.59627 CenterY=2.99743 CenterZ=0 NormalX=0 NormalY=0 NormalZ=1 AngleXU=0 Radius=1
    g6: Circle CenterX=-5.2 CenterY=1.5 CenterZ=0 NormalX=0 NormalY=0 NormalZ=1 AngleXU=0 Radius=1
    g7: BSplineCurve PolesCount=3 KnotsCount=2 Degree=2 IsPeriodic=0
    g8: GeomPoint X=-3.5 Y=4.7 Z=0
    g9: GeomPoint X=-5.2 Y=1.5 Z=0
  constraints (23):
    c: Vertical(g0)
    c: Distance(g0) = 3
    c: Coincident(g1,g0)
    c: Horizontal(g1)
    c: Block(g0)
    c: Block(g1)
    c: Coincident(g2,g0)
    c: Vertical(g2)
    c: Distance(g2) = 0.2
    c: Coincident(g3,g2)
    c: Horizontal(g3)
    c: Block(g3)
    c: Coincident(g7,g1)
    c: Weight(g4) = 1
    c: Equal(g4,g5)
    c: Equal(g4,g6)
    c: Coincident(g7,g3)
    c: InternalAlignment(g4,g7)
    c: InternalAlignment(g5,g7)
    c: InternalAlignment(g6,g7)
    c: InternalAlignment(g8,g7)
    c: InternalAlignment(g9,g7)
    c: Block(g7)
FEATURE [Sketcher::SketchObject] Sketch028
  FullyConstrained = true
  sketch-geometry (18):
    g0: LineSegment StartX=0 StartY=3e-16 StartZ=0 EndX=0 EndY=1.7 EndZ=0
    g1: LineSegment StartX=-3.5 StartY=0 StartZ=0 EndX=-3.5 EndY=0.9 EndZ=0
    g2: Circle CenterX=-2.7 CenterY=1.7 CenterZ=0 NormalX=0 NormalY=0 NormalZ=1 AngleXU=0 Radius=1
    g3: Circle CenterX=-3.5 CenterY=1.7 CenterZ=0 NormalX=0 NormalY=0 NormalZ=1 AngleXU=0 Radius=1
    g4: Circle CenterX=-3.5 CenterY=0.9 CenterZ=0 NormalX=0 NormalY=0 NormalZ=1 AngleXU=0 Radius=1
    g5: BSplineCurve PolesCount=3 KnotsCount=2 Degree=2 IsPeriodic=0
    g6: GeomPoint X=-2.7 Y=1.7 Z=0
    g7: GeomPoint X=-3.5 Y=0.9 Z=0
    g8: LineSegment StartX=-3.5 StartY=0 StartZ=0 EndX=-3.5 EndY=-7 EndZ=0
    g9: LineSegment StartX=0 StartY=3e-16 StartZ=0 EndX=0 EndY=-7 EndZ=0
    g10: LineSegment StartX=-3.5 StartY=-7 StartZ=0 EndX=0 EndY=-7 EndZ=0
    g11: LineSegment StartX=-2.7 StartY=1.7 StartZ=0 EndX=-1.6 EndY=1.7 EndZ=0
    g12: LineSegment StartX=0 StartY=1.7 StartZ=0 EndX=0 EndY=4.5 EndZ=0
    g13: LineSegment StartX=0 StartY=4.5 StartZ=0 EndX=0 EndY=10.8 EndZ=0
    g14: LineSegment StartX=0 StartY=10.8 StartZ=0 EndX=-2 EndY=10.8 EndZ=0
    g15: LineSegment StartX=-1.6 StartY=4.7 StartZ=0 EndX=-1.6 EndY=1.7 EndZ=0
    g16: LineSegment StartX=-1.6 StartY=4.7 StartZ=0 EndX=-2 EndY=4.7 EndZ=0
    g17: LineSegment StartX=-2 StartY=4.7 StartZ=0 EndX=-2 EndY=10.8 EndZ=0
  constraints (44):
    c: Vertical(g0)
    c: Vertical(g1)
    c: Distance(g1) = 0.9
    c: Block(g0)
    c: Distance(g0) = 1.7
    c: Weight(g2) = 1
    c: Equal(g2,g3)
    c: Equal(g2,g4)
    c: Coincident(g5,g1)
    c: InternalAlignment(g2,g5)
    c: InternalAlignment(g3,g5)
    c: InternalAlignment(g4,g5)
    c: InternalAlignment(g6,g5)
    c: InternalAlignment(g7,g5)
    c: Block(g5)
    c: Coincident(g8,g1)
    c: Vertical(g8)
    c: Distance(g8) = 7
    c: Vertical(g9)
    c: Equal(g8,g9) = 7
    c: Coincident(g9,g0)
    c: Coincident(g10,g8)
    c: Coincident(g10,g9)
    c: Horizontal(g10)
    c: Coincident(g11,g5)
    c: Horizontal(g11)
    c: Coincident(g12,g0)
    c: Vertical(g12)
    c: Distance(g12) = 2.8
    c: Coincident(g13,g12)
    c: Vertical(g13)
    c: Distance(g13) = 6.3
    c: Coincident(g14,g13)
    c: Horizontal(g14)
    c: Distance(g14) = 2
    c: Vertical(g15)
    c: Distance(g15) = 3
    c: Block(g11)
    c: Coincident(g15,g11)
    c: Coincident(g16,g15)
    c: Horizontal(g16)
    c: Coincident(g17,g16)
    c: Coincident(g17,g14)
    c: Vertical(g17)
FEATURE [Part::Revolution] Revolve040  label="backCaseScrewRetainer001"
  Angle = 360
  Axis = (0,1,0)
  Base = (0,0,0)
  FaceMakerClass = Part::FaceMakerBullseye
  Placement = pos=(12.5,3,10) rot=(0,0,1;0rad)
  Solid = false
  Source = -> Face036
  Symmetric = false
FEATURE [Part::Feature] Face055
  shape: bbox 3.5 x 30.2 x 2e-07 mm, 1 faces, 0 solids (baked)
FEATURE [Part::Revolution] Revolve059  label="backCaseScrewPost"
  Angle = 360
  Axis = (0,1,0)
  Base = (0,0,0)
  FaceMakerClass = Part::FaceMakerBullseye
  Placement = pos=(12.5,4.5,10) rot=(0,0,1;0rad)
  Solid = false
  Source = -> Face055
  Symmetric = false
FEATURE [Part::Feature] Face056
  shape: bbox 3.5 x 30.2 x 2e-07 mm, 1 faces, 0 solids (baked)
FEATURE [Part::Revolution] Revolve060  label="backCaseScrewPost001"
  Angle = 360
  Axis = (0,1,0)
  Base = (0,0,0)
  FaceMakerClass = Part::FaceMakerBullseye
  Placement = pos=(12.5,4.5,62) rot=(0,0,1;0rad)
  Solid = false
  Source = -> Face056
  Symmetric = false
FEATURE [Part::Feature] Face057
  shape: bbox 3.5 x 17.8 x 2e-07 mm, 1 faces, 0 solids (baked)
FEATURE [Part::Revolution] Revolve061  label="removeToCreateScrewAndThreadedInsertHole"
  Angle = 360
  Axis = (0,1,0)
  Base = (0,0,0)
  FaceMakerClass = Part::FaceMakerBullseye
  Placement = pos=(12.5,0,10) rot=(0,0,1;0rad)
  Solid = false
  Source = -> Face057
  Symmetric = false
FEATURE [Part::Feature] Face058
  shape: bbox 3.5 x 17.8 x 2e-07 mm, 1 faces, 0 solids (baked)
FEATURE [Part::Revolution] Revolve062  label="removeToCreateScrewAndThreadedInsertHole001"
  Angle = 360
  Axis = (0,1,0)
  Base = (0,0,0)
  FaceMakerClass = Part::FaceMakerBullseye
  Placement = pos=(12.5,0,62) rot=(0,0,1;0rad)
  Solid = false
  Source = -> Face058
  Symmetric = false
FEATURE [Part::Feature] Face059
  shape: bbox 3.5 x 17.8 x 2e-07 mm, 1 faces, 0 solids (baked)
FEATURE [Part::Revolution] Revolve063  label="removeToCreateScrewAndThreadedInsertHole002"
  Angle = 360
  Axis = (0,1,0)
  Base = (0,0,0)
  FaceMakerClass = Part::FaceMakerBullseye
  Placement = pos=(89.5,0,68.5) rot=(0,0,1;0rad)
  Solid = false
  Source = -> Face059
  Symmetric = false
FEATURE [Part::Feature] Face060
  shape: bbox 3.5 x 17.8 x 2e-07 mm, 1 faces, 0 solids (baked)
FEATURE [Part::Revolution] Revolve064  label="removeToCreateScrewAndThreadedInsertHole003"
  Angle = 360
  Axis = (0,1,0)
  Base = (0,0,0)
  FaceMakerClass = Part::FaceMakerBullseye
  Placement = pos=(89.5,0,3.5) rot=(0,0,1;0rad)
  Solid = false
  Source = -> Face060
  Symmetric = false
FEATURE [Part::Feature] Face061
  shape: bbox 3.5 x 17.8 x 2e-07 mm, 1 faces, 0 solids (baked)
FEATURE [Part::Revolution] Revolve065  label="removeToCreateScrewAndThreadedInsertHole004"
  Angle = 360
  Axis = (0,1,0)
  Base = (0,0,0)
  FaceMakerClass = Part::FaceMakerBullseye
  Placement = pos=(102.5,4.7,3.5) rot=(0,0,1;0rad)
  Solid = false
  Source = -> Face061
  Symmetric = false
FEATURE [Part::Feature] Face062
  shape: bbox 3.5 x 17.8 x 2e-07 mm, 1 faces, 0 solids (baked)
FEATURE [Part::Revolution] Revolve066  label="removeToCreateScrewAndThreadedInsertHole005"
  Angle = 360
  Axis = (0,1,0)
  Base = (0,0,0)
  FaceMakerClass = Part::FaceMakerBullseye
  Placement = pos=(102.5,4.7,68.5) rot=(0,0,1;0rad)
  Solid = false
  Source = -> Face062
  Symmetric = false
FEATURE [Part::MultiFuse] Fusion047  label="makeHoles"
  Shapes = -> [Revolve066,Revolve065,Revolve064,Revolve063,Revolve062,Revolve061]
FEATURE [Part::Feature] Face063
  shape: bbox 3.6 x 3.2 x 2e-07 mm, 1 faces, 0 solids (baked)
FEATURE [Part::Revolution] Revolve067  label="moreFrontCaseScrewRetainer002"
  Angle = 360
  Axis = (0,1,0)
  Base = (0,0,0)
  FaceMakerClass = Part::FaceMakerBullseye
  Placement = pos=(102.5,4.5,68.5) rot=(0,0,1;0rad)
  Solid = false
  Source = -> Face063
  Symmetric = false
FEATURE [Part::Feature] Face064
  shape: bbox 3.6 x 3.2 x 2e-07 mm, 1 faces, 0 solids (baked)
FEATURE [Part::Revolution] Revolve068  label="moreFrontCaseScrewRetainer003"
  Angle = 360
  Axis = (0,1,0)
  Base = (0,0,0)
  FaceMakerClass = Part::FaceMakerBullseye
  Placement = pos=(102.5,4.5,3.5) rot=(0,0,1;0rad)
  Solid = false
  Source = -> Face064
  Symmetric = false
FEATURE [Part::Cut] Cut014  label="bottom003"
  Base = -> Cut007
  Tool = -> Fusion047
FEATURE [Part::Feature] Face065
  shape: bbox 3.5 x 17.8 x 2e-07 mm, 1 faces, 0 solids (baked)
FEATURE [Part::Revolution] Revolve069  label="removeToCreateScrewAndThreadedInsertHole006"
  Angle = 360
  Axis = (0,1,0)
  Base = (0,0,0)
  FaceMakerClass = Part::FaceMakerBullseye
  Placement = pos=(12.5,0,10) rot=(0,0,1;0rad)
  Solid = false
  Source = -> Face065
  Symmetric = false
FEATURE [Part::Feature] Face066
  shape: bbox 3.5 x 17.8 x 2e-07 mm, 1 faces, 0 solids (baked)
FEATURE [Part::Revolution] Revolve070  label="removeToCreateScrewAndThreadedInsertHole007"
  Angle = 360
  Axis = (0,1,0)
  Base = (0,0,0)
  FaceMakerClass = Part::FaceMakerBullseye
  Placement = pos=(12.5,0,62) rot=(0,0,1;0rad)
  Solid = false
  Source = -> Face066
  Symmetric = false
FEATURE [Part::Feature] Face067
  shape: bbox 3.5 x 17.8 x 2e-07 mm, 1 faces, 0 solids (baked)
FEATURE [Part::Revolution] Revolve071  label="removeToCreateScrewAndThreadedInsertHole008"
  Angle = 360
  Axis = (0,1,0)
  Base = (0,0,0)
  FaceMakerClass = Part::FaceMakerBullseye
  Placement = pos=(89.5,0,68.5) rot=(0,0,1;0rad)
  Solid = false
  Source = -> Face067
  Symmetric = false
FEATURE [Part::Feature] Face068
  shape: bbox 3.5 x 17.8 x 2e-07 mm, 1 faces, 0 solids (baked)
FEATURE [Part::Revolution] Revolve072  label="removeToCreateScrewAndThreadedInsertHole009"
  Angle = 360
  Axis = (0,1,0)
  Base = (0,0,0)
  FaceMakerClass = Part::FaceMakerBullseye
  Placement = pos=(89.5,0,3.5) rot=(0,0,1;0rad)
  Solid = false
  Source = -> Face068
  Symmetric = false
FEATURE [Part::Feature] Face069
  shape: bbox 3.5 x 17.8 x 2e-07 mm, 1 faces, 0 solids (baked)
FEATURE [Part::Feature] Face070
  shape: bbox 3.5 x 17.8 x 2e-07 mm, 1 faces, 0 solids (baked)
FEATURE [Part::Revolution] Revolve073  label="removeToCreateScrewAndThreadedInsertHole010"
  Angle = 360
  Axis = (0,1,0)
  Base = (0,0,0)
  FaceMakerClass = Part::FaceMakerBullseye
  Placement = pos=(102.5,4.7,3.5) rot=(0,0,1;0rad)
  Solid = false
  Source = -> Face069
  Symmetric = false
FEATURE [Part::Revolution] Revolve074  label="removeToCreateScrewAndThreadedInsertHole011"
  Angle = 360
  Axis = (0,1,0)
  Base = (0,0,0)
  FaceMakerClass = Part::FaceMakerBullseye
  Placement = pos=(102.5,4.7,68.5) rot=(0,0,1;0rad)
  Solid = false
  Source = -> Face070
  Symmetric = false
FEATURE [Part::MultiFuse] Fusion048  label="makeHoles001"
  Shapes = -> [Revolve074,Revolve073,Revolve072,Revolve071,Revolve070,Revolve069]
FEATURE [Part::MultiFuse] Fusion049  label="caseScrewRetainers"
  Shapes = -> [Revolve067,Revolve068,Revolve048,Revolve047,Revolve039,Revolve040]
FEATURE [Part::Cut] Cut015  label="caseScrewRetainers001"
  Base = -> Fusion049
  Tool = -> Fusion048
FEATURE [Part::MultiFuse] Fusion050  label="casePillars"
  Shapes = -> [Revolve055,Revolve054,Revolve043,Revolve046,Revolve059,Revolve060]
FEATURE [Part::Feature] Face071 .. Face076  x6 (patterned run collapsed; names and placements below)
  shape: bbox 3.5 x 17.8 x 2e-07 mm, 1 faces, 0 solids (baked)
FEATURE [Part::Revolution] Revolve075  label="removeToCreateScrewAndThreadedInsertHole012"
  Angle = 360
  Axis = (0,1,0)
  Base = (0,0,0)
  FaceMakerClass = Part::FaceMakerBullseye
  Placement = pos=(12.5,0,10) rot=(0,0,1;0rad)
  Solid = false
  Source = -> Face071
  Symmetric = false
FEATURE [Part::Revolution] Revolve076  label="removeToCreateScrewAndThreadedInsertHole013"
  Angle = 360
  Axis = (0,1,0)
  Base = (0,0,0)
  FaceMakerClass = Part::FaceMakerBullseye
  Placement = pos=(12.5,0,62) rot=(0,0,1;0rad)
  Solid = false
  Source = -> Face072
  Symmetric = false
FEATURE [Part::Revolution] Revolve077  label="removeToCreateScrewAndThreadedInsertHole014"
  Angle = 360
  Axis = (0,1,0)
  Base = (0,0,0)
  FaceMakerClass = Part::FaceMakerBullseye
  Placement = pos=(89.5,0,68.5) rot=(0,0,1;0rad)
  Solid = false
  Source = -> Face073
  Symmetric = false
FEATURE [Part::Revolution] Revolve078  label="removeToCreateScrewAndThreadedInsertHole015"
  Angle = 360
  Axis = (0,1,0)
  Base = (0,0,0)
  FaceMakerClass = Part::FaceMakerBullseye
  Placement = pos=(89.5,0,3.5) rot=(0,0,1;0rad)
  Solid = false
  Source = -> Face074
  Symmetric = false
FEATURE [Part::Revolution] Revolve079  label="removeToCreateScrewAndThreadedInsertHole016"
  Angle = 360
  Axis = (0,1,0)
  Base = (0,0,0)
  FaceMakerClass = Part::FaceMakerBullseye
  Placement = pos=(102.5,4.7,3.5) rot=(0,0,1;0rad)
  Solid = false
  Source = -> Face075
  Symmetric = false
FEATURE [Part::Revolution] Revolve080  label="removeToCreateScrewAndThreadedInsertHole017"
  Angle = 360
  Axis = (0,1,0)
  Base = (0,0,0)
  FaceMakerClass = Part::FaceMakerBullseye
  Placement = pos=(102.5,4.7,68.5) rot=(0,0,1;0rad)
  Solid = false
  Source = -> Face076
  Symmetric = false
FEATURE [Part::MultiFuse] Fusion051  label="makeHoles002"
  Shapes = -> [Revolve080,Revolve079,Revolve078,Revolve077,Revolve076,Revolve075]
FEATURE [Part::Cut] Cut016  label="caesPillars"
  Base = -> Fusion050
  Tool = -> Fusion051
FEATURE [Part::Revolution] Revolve009  label="plugHousing016"
  Angle = 360
  Axis = (0,1,0)
  Base = (0,0,0)
  FaceMakerClass = Part::FaceMakerBullseye
  Placement = pos=(0,0,36.15) rot=(0,0,1;0rad)
  Solid = false
  Source = -> Face012
  Symmetric = false
FEATURE [Part::MultiFuse] Fusion014  label="plugHousing023"
  Placement = pos=(0,0,0) rot=(0,0,1;1.5708rad)
  Shapes = -> [Revolve011,Revolve009]
FEATURE [Part::Revolution] Revolve010  label="plugHousing017"
  Angle = 360
  Axis = (0,1,0)
  Base = (0,0,0)
  FaceMakerClass = Part::FaceMakerBullseye
  Placement = pos=(0,0,36.15) rot=(0,0,1;0rad)
  Solid = false
  Source = -> Face014
  Symmetric = false
FEATURE [Part::MultiFuse] Fusion015  label="plugHousing024"
  Placement = pos=(0,0,0) rot=(0,0,1;1.5708rad)
  Shapes = -> [Revolve010,Revolve015]
FEATURE [Part::Revolution] Revolve014  label="plugHousing026"
  Angle = 360
  Axis = (0,1,0)
  Base = (0,0,0)
  FaceMakerClass = Part::FaceMakerBullseye
  Placement = pos=(0,0,36.15) rot=(0,0,1;0rad)
  Solid = false
  Source = -> Face011
  Symmetric = false
FEATURE [Part::Revolution] Revolve013  label="plugHousing025"
  Angle = 360
  Axis = (0,1,0)
  Base = (0,0,0)
  FaceMakerClass = Part::FaceMakerBullseye
  Placement = pos=(0,0,36.15) rot=(0,0,1;0rad)
  Solid = false
  Source = -> Face015
  Symmetric = false
FEATURE [Part::MultiFuse] Fusion016  label="plugHousing028"
  Placement = pos=(0,19,0) rot=(0,0,1;3.14159rad)
  Shapes = -> [Fusion014,Fusion013]
FEATURE [Part::MultiFuse] Fusion011  label="plugHousing018"
  Placement = pos=(0,0,0) rot=(0,0,1;1.5708rad)
  Shapes = -> [Revolve014,Revolve013]
FEATURE [Part::MultiFuse] Fusion012  label="plugHousing019"
  Placement = pos=(0,19,0) rot=(0,0,1;3.14159rad)
  Shapes = -> [Fusion011,Fusion015]
FEATURE [Part::MultiFuse] Fusion017  label="plugHousing029"
  Placement = pos=(122.621,0,-0.15) rot=(0,0,1;0rad)
  Shapes = -> [Fusion016,Fusion012]
FEATURE [Part::MultiFuse] Fusion052  label="casePillarRetainers"
  Shapes = -> [Extrude012,Extrude013,Extrude014,Extrude015,Extrude016,Extrude017,Extrude018,Extrude019,Box011,Box012]
FEATURE [Part::Feature] Face077
  shape: bbox 3.5 x 17.8 x 2e-07 mm, 1 faces, 0 solids (baked)
FEATURE [Part::Revolution] Revolve081  label="removeToCreateScrewAndThreadedInsertHole018"
  Angle = 360
  Axis = (0,1,0)
  Base = (0,0,0)
  FaceMakerClass = Part::FaceMakerBullseye
  Placement = pos=(62.3,30.3,19.7) rot=(0,0,1;0rad)
  Solid = false
  Source = -> Face077
  Symmetric = false
FEATURE [Part::Feature] Face078
  shape: bbox 3.5 x 17.8 x 2e-07 mm, 1 faces, 0 solids (baked)
FEATURE [Part::Revolution] Revolve082  label="removeToCreateScrewAndThreadedInsertHole019"
  Angle = 360
  Axis = (0,1,0)
  Base = (0,0,0)
  FaceMakerClass = Part::FaceMakerBullseye
  Placement = pos=(62.3,30.3,51.7) rot=(0,0,1;0rad)
  Solid = false
  Source = -> Face078
  Symmetric = false
FEATURE [Part::Feature] Face079
  shape: bbox 3.5 x 17.8 x 2e-07 mm, 1 faces, 0 solids (baked)
FEATURE [Part::Revolution] Revolve083  label="removeToCreateScrewAndThreadedInsertHole020"
  Angle = 360
  Axis = (0,1,0)
  Base = (0,0,0)
  FaceMakerClass = Part::FaceMakerBullseye
  Placement = pos=(30.3,30.3,19.7) rot=(0,0,1;0rad)
  Solid = false
  Source = -> Face079
  Symmetric = false
FEATURE [Part::Feature] Face080
  shape: bbox 3.5 x 17.8 x 2e-07 mm, 1 faces, 0 solids (baked)
FEATURE [Part::Revolution] Revolve084  label="removeToCreateScrewAndThreadedInsertHole021"
  Angle = 360
  Axis = (0,1,0)
  Base = (0,0,0)
  FaceMakerClass = Part::FaceMakerBullseye
  Placement = pos=(30.3,30.3,51.7) rot=(0,0,1;0rad)
  Solid = false
  Source = -> Face080
  Symmetric = false
FEATURE [Part::MultiFuse] Fusion053  label="createThreadedInsertHolesForFan"
  Shapes = -> [Revolve081,Revolve082,Revolve083,Revolve084]
FEATURE [Part::Cut] Cut017  label="fanScrewHousing001"
  Base = -> Fusion046
  Tool = -> Fusion053
FEATURE [Part::Feature] Face081
  shape: bbox 3.5 x 17.8 x 2e-07 mm, 1 faces, 0 solids (baked)
FEATURE [Part::Revolution] Revolve085  label="removeToCreateScrewAndThreadedInsertHole022"
  Angle = 360
  Axis = (0,1,0)
  Base = (0,0,0)
  FaceMakerClass = Part::FaceMakerBullseye
  Placement = pos=(62.3,30.3,19.7) rot=(0,0,1;0rad)
  Solid = false
  Source = -> Face081
  Symmetric = false
FEATURE [Part::Feature] Face082
  shape: bbox 3.5 x 17.8 x 2e-07 mm, 1 faces, 0 solids (baked)
FEATURE [Part::Revolution] Revolve086  label="removeToCreateScrewAndThreadedInsertHole023"
  Angle = 360
  Axis = (0,1,0)
  Base = (0,0,0)
  FaceMakerClass = Part::FaceMakerBullseye
  Placement = pos=(62.3,30.3,51.7) rot=(0,0,1;0rad)
  Solid = false
  Source = -> Face082
  Symmetric = false
FEATURE [Part::Feature] Face083
  shape: bbox 3.5 x 17.8 x 2e-07 mm, 1 faces, 0 solids (baked)
FEATURE [Part::Revolution] Revolve087  label="removeToCreateScrewAndThreadedInsertHole024"
  Angle = 360
  Axis = (0,1,0)
  Base = (0,0,0)
  FaceMakerClass = Part::FaceMakerBullseye
  Placement = pos=(30.3,30.3,19.7) rot=(0,0,1;0rad)
  Solid = false
  Source = -> Face083
  Symmetric = false
FEATURE [Part::Feature] Face084
  shape: bbox 3.5 x 17.8 x 2e-07 mm, 1 faces, 0 solids (baked)
FEATURE [Part::Revolution] Revolve088  label="removeToCreateScrewAndThreadedInsertHole025"
  Angle = 360
  Axis = (0,1,0)
  Base = (0,0,0)
  FaceMakerClass = Part::FaceMakerBullseye
  Placement = pos=(30.3,30.3,51.7) rot=(0,0,1;0rad)
  Solid = false
  Source = -> Face084
  Symmetric = false
FEATURE [Part::MultiFuse] Fusion054  label="createThreadedInsertHolesForFan001"
  Shapes = -> [Revolve085,Revolve086,Revolve087,Revolve088]
FEATURE [Part::Cut] Cut018  label="top007"
  Base = -> Fusion040
  Tool = -> Fusion054
FEATURE [Sketcher::SketchObject] Sketch029
  FullyConstrained = false
  Placement = pos=(0,0,0) rot=(-1,0,0;4.71239rad)
  sketch-geometry (72):
    g0: LineSegment StartX=0 StartY=0 StartZ=0 EndX=-38.2 EndY=0 EndZ=0
    g1: LineSegment StartX=0 StartY=0 StartZ=0 EndX=0 EndY=-38.2 EndZ=0
    g2: LineSegment StartX=0 StartY=-38.2 StartZ=0 EndX=-38.2 EndY=-38.2 EndZ=0
    g3: LineSegment StartX=-38.2 StartY=0 StartZ=0 EndX=-38.2 EndY=-38.2 EndZ=0
    g4: LineSegment StartX=-38.2 StartY=-38.2 StartZ=0 EndX=-35.7 EndY=-38.2 EndZ=0
    g5: LineSegment StartX=-38.2 StartY=0 StartZ=0 EndX=-35.7 EndY=0 EndZ=0
    g6: LineSegment StartX=0 StartY=0 StartZ=0 EndX=-2.5 EndY=0 EndZ=0
    g7: LineSegment StartX=0 StartY=-38.2 StartZ=0 EndX=-2.5 EndY=-38.2 EndZ=0
    g8: LineSegment StartX=-2.5 StartY=0 StartZ=0 EndX=-2.5 EndY=-9 EndZ=0
    g9: LineSegment StartX=-35.7 StartY=0 StartZ=0 EndX=-35.7 EndY=-9 EndZ=0
    g10: LineSegment StartX=-35.7 StartY=-38.2 StartZ=0 EndX=-35.7 EndY=-29.2 EndZ=0
    g11: LineSegment StartX=-2.5 StartY=-38.2 StartZ=0 EndX=-2.5 EndY=-29.2 EndZ=0
    g12: LineSegment StartX=-5.5 StartY=-10.5 StartZ=0 EndX=-4 EndY=-10.5 EndZ=0
    g13: LineSegment StartX=-4 StartY=-10.5 StartZ=0 EndX=-2.5 EndY=-10.5 EndZ=0
    g14: ArcOfCircle CenterX=-4 CenterY=-10.5 CenterZ=0 NormalX=0 NormalY=0 NormalZ=1 AngleXU=0 Radius=1.5 StartAngle=6e-16 EndAngle=3.14159
    g15: LineSegment StartX=-35.7 StartY=-9 StartZ=0 EndX=-35.7 EndY=-10.5 EndZ=0
    g16: LineSegment StartX=-32.7 StartY=-10.5 StartZ=0 EndX=-34.2 EndY=-10.5 EndZ=0
    g17: ArcOfCircle CenterX=-34.2 CenterY=-10.5 CenterZ=0 NormalX=0 NormalY=0 NormalZ=1 AngleXU=0 Radius=1.5 StartAngle=0 EndAngle=3.14159
    g18: LineSegment StartX=-2.5 StartY=-9 StartZ=0 EndX=-2.5 EndY=-10.5 EndZ=0
    g19: LineSegment StartX=-34.2 StartY=-10.5 StartZ=0 EndX=-35.7 EndY=-10.5 EndZ=0
    g20: LineSegment StartX=-32.7 StartY=-10.5 StartZ=0 EndX=-29.7 EndY=-10.5 EndZ=0
    g21: LineSegment StartX=-29.7 StartY=-10.5 StartZ=0 EndX=-26.7 EndY=-10.5 EndZ=0
    g22: LineSegment StartX=-26.7 StartY=-10.5 StartZ=0 EndX=-23.6 EndY=-10.5 EndZ=0
    g23: LineSegment StartX=-23.6 StartY=-10.5 StartZ=0 EndX=-20.6 EndY=-10.5 EndZ=0
    g24: LineSegment StartX=-20.6 StartY=-10.5 StartZ=0 EndX=-17.6 EndY=-10.5 EndZ=0
    g25: LineSegment StartX=-17.6 StartY=-10.5 StartZ=0 EndX=-14.6 EndY=-10.5 EndZ=0
    g26: LineSegment StartX=-14.6 StartY=-10.5 StartZ=0 EndX=-11.5 EndY=-10.5 EndZ=0
    g27: LineSegment StartX=-11.5 StartY=-10.5 StartZ=0 EndX=-8.5 EndY=-10.5 EndZ=0
    g28: LineSegment StartX=-8.5 StartY=-10.5 StartZ=0 EndX=-5.5 EndY=-10.5 EndZ=0
    g29: LineSegment StartX=-35.7 StartY=-10.5 StartZ=0 EndX=-35.7 EndY=-27.7 EndZ=0
    g30: LineSegment StartX=-2.5 StartY=-27.7 StartZ=0 EndX=-2.5 EndY=-10.5 EndZ=0
    g31: LineSegment StartX=-14.4973 StartY=-10.5 StartZ=0 EndX=-11.4973 EndY=-10.5 EndZ=0
    g32: ArcOfCircle CenterX=-34.2 CenterY=-27.7 CenterZ=0 NormalX=0 NormalY=0 NormalZ=1 AngleXU=0 Radius=1.5 StartAngle=3.14159 EndAngle=6.28319
    g33: LineSegment StartX=-35.7 StartY=-27.7 StartZ=0 EndX=-35.7 EndY=-29.2 EndZ=0
    g34: ArcOfCircle CenterX=-4 CenterY=-27.7 CenterZ=0 NormalX=0 NormalY=0 NormalZ=1 AngleXU=0 Radius=1.5 StartAngle=3.1416 EndAngle=6.28319
    g35: LineSegment StartX=-5.5 StartY=-27.7 StartZ=0 EndX=-5.5 EndY=-10.5 EndZ=0
    g36: LineSegment StartX=-38.2 StartY=0 StartZ=0 EndX=0 EndY=-38.2 EndZ=0
    g37: LineSegment StartX=-38.2 StartY=-38.2 StartZ=0 EndX=0 EndY=0 EndZ=0
    g38: Circle CenterX=-19.1993 CenterY=-19.1993 CenterZ=0 NormalX=0 NormalY=0 NormalZ=1 AngleXU=0 Radius=17.5127
    g39: LineSegment StartX=-11.5 StartY=-10.5 StartZ=0 EndX=-11.5 EndY=-4.3 EndZ=0
    g40: LineSegment StartX=-8.5 StartY=-10.5 StartZ=0 EndX=-8.5 EndY=-4.3 EndZ=0
    g41: LineSegment StartX=-14.6 StartY=-10.5 StartZ=0 EndX=-14.6 EndY=-1.8 EndZ=0
    g42: ArcOfCircle CenterX=-10 CenterY=-4.3 CenterZ=0 NormalX=0 NormalY=0 NormalZ=1 AngleXU=0 Radius=1.5 StartAngle=2e-16 EndAngle=3.14159
    g43: ArcOfCircle CenterX=-16.1 CenterY=-1.8 CenterZ=0 NormalX=0 NormalY=0 NormalZ=1 AngleXU=0 Radius=1.5 StartAngle=5e-16 EndAngle=3.14159
    g44: LineSegment StartX=-17.6 StartY=-10.5 StartZ=0 EndX=-17.6 EndY=-1.8 EndZ=0
    g45: LineSegment StartX=-20.6 StartY=-10.5 StartZ=0 EndX=-20.6 EndY=-1.8 EndZ=0
    g46: LineSegment StartX=-23.6 StartY=-10.5 StartZ=0 EndX=-23.6 EndY=-1.8 EndZ=0
    g47: ArcOfCircle CenterX=-22.1 CenterY=-1.8 CenterZ=0 NormalX=0 NormalY=0 NormalZ=1 AngleXU=0 Radius=1.5 StartAngle=5e-16 EndAngle=3.14159
    g48: LineSegment StartX=-26.7 StartY=-10.5 StartZ=0 EndX=-26.7 EndY=-4.3 EndZ=0
    g49: LineSegment StartX=-29.7 StartY=-10.5 StartZ=0 EndX=-29.7 EndY=-4.3 EndZ=0
    g50: ArcOfCircle CenterX=-28.2 CenterY=-4.3 CenterZ=0 NormalX=0 NormalY=0 NormalZ=1 AngleXU=0 Radius=1.5 StartAngle=2e-16 EndAngle=3.14159
    g51: LineSegment StartX=-29.7 StartY=-10.5 StartZ=0 EndX=-29.7 EndY=-27.7 EndZ=0
    g52: LineSegment StartX=-26.7 StartY=-10.5 StartZ=0 EndX=-26.7 EndY=-27.7 EndZ=0
    g53: LineSegment StartX=-23.6 StartY=-10.5 StartZ=0 EndX=-23.6 EndY=-27.7 EndZ=0
    g54: LineSegment StartX=-20.6 StartY=-10.5 StartZ=0 EndX=-20.6 EndY=-27.7 EndZ=0
    g55: LineSegment StartX=-32.7 StartY=-10.5 StartZ=0 EndX=-32.7 EndY=-27.7 EndZ=0
    g56: LineSegment StartX=-17.6 StartY=-10.5 StartZ=0 EndX=-17.6 EndY=-27.7 EndZ=0
    g57: LineSegment StartX=-14.6 StartY=-10.5 StartZ=0 EndX=-14.6 EndY=-27.7 EndZ=0
    g58: LineSegment StartX=-11.5 StartY=-10.5 StartZ=0 EndX=-11.5 EndY=-27.7 EndZ=0
    g59: LineSegment StartX=-8.5 StartY=-10.5 StartZ=0 EndX=-8.5 EndY=-27.7 EndZ=0
    g60: LineSegment StartX=-11.5 StartY=-27.7 StartZ=0 EndX=-11.5 EndY=-33.9 EndZ=0
    g61: LineSegment StartX=-8.5 StartY=-27.7 StartZ=0 EndX=-8.5 EndY=-33.9 EndZ=0
    g62: LineSegment StartX=-26.7 StartY=-27.7 StartZ=0 EndX=-26.7 EndY=-33.9 EndZ=0
    g63: LineSegment StartX=-29.7 StartY=-27.7 StartZ=0 EndX=-29.7 EndY=-33.9 EndZ=0
    g64: LineSegment StartX=-14.6 StartY=-27.7 StartZ=0 EndX=-14.6 EndY=-36.4 EndZ=0
    g65: LineSegment StartX=-17.6 StartY=-27.7 StartZ=0 EndX=-17.6 EndY=-36.4 EndZ=0
    g66: LineSegment StartX=-20.6 StartY=-27.7 StartZ=0 EndX=-20.6 EndY=-36.4 EndZ=0
    g67: LineSegment StartX=-23.6 StartY=-27.7 StartZ=0 EndX=-23.6 EndY=-36.4 EndZ=0
    g68: ArcOfCircle CenterX=-10 CenterY=-33.9 CenterZ=0 NormalX=0 NormalY=0 NormalZ=1 AngleXU=0 Radius=1.5 StartAngle=3.14159 EndAngle=6.28319
    g69: ArcOfCircle CenterX=-16.1 CenterY=-36.4 CenterZ=0 NormalX=0 NormalY=0 NormalZ=1 AngleXU=0 Radius=1.5 StartAngle=3.14159 EndAngle=6.28319
    g70: ArcOfCircle CenterX=-22.1 CenterY=-36.4 CenterZ=0 NormalX=0 NormalY=0 NormalZ=1 AngleXU=0 Radius=1.5 StartAngle=3.14159 EndAngle=6.28319
    g71: ArcOfCircle CenterX=-28.2 CenterY=-33.9 CenterZ=0 NormalX=0 NormalY=0 NormalZ=1 AngleXU=0 Radius=1.5 StartAngle=3.14159 EndAngle=6.28319
  constraints (202):
    c: Coincident(g0,g-1)
    c: Horizontal(g0)
    c: Distance(g0) = 38.2
    c: Coincident(g1,g0)
    c: Vertical(g1)
    c: Distance(g1) = 38.2
    c: Horizontal(g2)
    c: Equal(g0,g2) = 38.2
    c: Coincident(g2,g1)
    c: Vertical(g3)
    c: Equal(g1,g3) = 38.2
    c: Coincident(g3,g0)
    c: Horizontal(g4)
    c: Coincident(g4,g2)
    c: Horizontal(g5)
    c: Coincident(g5,g0)
    c: Horizontal(g6)
    c: Coincident(g6,g0)
    c: Horizontal(g7)
    c: Coincident(g7,g1)
    c: Coincident(g8,g6)
    c: Vertical(g8)
    c: Distance(g8) = 9
    c: Vertical(g9)
    c: Equal(g8,g9) = 9
    c: Coincident(g9,g5)
    c: Coincident(g10,g4)
    c: Vertical(g10)
    c: Distance(g10) = 9
    c: Vertical(g11)
    c: Equal(g10,g11) = 9
    c: Coincident(g11,g7)
    c: Block(g0)
    c: Block(g8)
    c: Block(g9)
    c: Block(g11)
    c: Block(g10)
    c: Horizontal(g12)
    c: Distance(g12) = 1.5
    c: Horizontal(g13)
    c: Equal(g12,g13) = 1.5
    c: Coincident(g13,g12)
    c: Coincident(g14,g12)
    c: Coincident(g14,g13)
    c: Block(g14)
    c: Coincident(g15,g9)
    c: Vertical(g15)
    c: Distance(g15) = 1.5
    c: Horizontal(g16)
    c: Coincident(g17,g16)
    c: Block(g17)
    c: Coincident(g18,g8)
    c: Coincident(g18,g13)
    c: Vertical(g18)
    c: Distance(g16) = 1.5
    c: Horizontal(g19)
    c: Equal(g16,g19) = 1.5
    c: Coincident(g19,g16)
    c: Horizontal(g20)
    c: Coincident(g20,g16)
    c: Horizontal(g21)
    c: Coincident(g21,g20)
    c: Horizontal(g22)
    c: Distance(g22) = 3.1
    c: Coincident(g22,g21)
    c: Horizontal(g23)
    c: Coincident(g23,g22)
    c: Horizontal(g24)
    c: Coincident(g24,g23)
    c: Horizontal(g25)
    c: Coincident(g25,g24)
    c: Horizontal(g26)
    c: Coincident(g26,g25)
    c: Horizontal(g27)
    c: Coincident(g27,g26)
    c: Distance(g26) = 3.1
    c: Coincident(g28,g27)
    c: Coincident(g28,g12)
    c: Horizontal(g28)
    c: Distance(g28) = 3
    c: Distance(g20) = 3
    c: Distance(g21) = 3
    c: Distance(g23) = 3
    c: Distance(g24) = 3
    c: Distance(g25) = 3
    c: Distance(g27) = 3
    c: Coincident(g29,g15)
    c: Vertical(g29)
    c: Distance(g10) = 9
    c: Distance(g10) = 9
    c: Distance(g9) = 9
    c: Coincident(g30,g13)
    c: Vertical(g30)
    c: Distance(g30) = 17.2
    c: Horizontal(g31)
    c: Equal(g27,g31) = 3
    c: Block(g29)
    c: Coincident(g33,g10)
    c: Vertical(g33)
    c: Block(g32)
    c: Block(g34)
    c: Coincident(g35,g34)
    c: Coincident(g35,g12)
    c: Vertical(g35)
    c: Coincident(g36,g0)
    c: Coincident(g36,g1)
    c: Coincident(g37,g2)
    c: Coincident(g37,g0)
    c: PointOnObject(g38,g37)
    c: PointOnObject(g12,g38)
    c: Coincident(g39,g26)
    c: Vertical(g39)
    c: Distance(g39) = 6.2
    c: Vertical(g40)
    c: Equal(g39,g40) = 5.5
    c: Coincident(g40,g27)
    c: Coincident(g41,g25)
    c: Vertical(g41)
    c: Distance(g41) = 8.7
    c: Block(g42)
    c: Coincident(g42,g40)
    c: Block(g43)
    c: Coincident(g43,g41)
    c: Vertical(g44)
    c: Equal(g41,g44) = 8.2
    c: Coincident(g44,g24)
    c: Vertical(g45)
    c: Equal(g41,g45) = 8.2
    c: Coincident(g45,g23)
    c: Vertical(g46)
    c: Equal(g41,g46) = 8.2
    c: Coincident(g46,g22)
    c: Block(g47)
    c: Coincident(g47,g45)
    c: Vertical(g48)
    c: Coincident(g48,g21)
    c: Vertical(g49)
    c: Coincident(g49,g20)
    c: Block(g48)
    c: Block(g49)
    c: Block(g50)
    c: Coincident(g50,g48)
    c: Vertical(g51)
    c: Block(g51)
    c: Coincident(g51,g20)
    c: Vertical(g52)
    c: Block(g52)
    c: Coincident(g52,g21)
    c: Vertical(g53)
    c: Block(g53)
    c: Coincident(g53,g22)
    c: Vertical(g54)
    c: Block(g54)
    c: Coincident(g54,g23)
    c: Vertical(g55)
    c: Block(g55)
    c: Coincident(g55,g16)
    c: Vertical(g56)
    c: Block(g56)
    c: Coincident(g56,g24)
    c: Vertical(g57)
    c: Block(g57)
    c: Coincident(g57,g25)
    c: Vertical(g58)
    c: Block(g58)
    c: Coincident(g58,g26)
    c: Vertical(g59)
    c: Block(g59)
    c: Coincident(g59,g27)
    c: Vertical(g60)
    c: Coincident(g60,g58)
    c: Vertical(g61)
    c: Coincident(g61,g59)
    c: Vertical(g62)
    c: Coincident(g62,g52)
    c: Vertical(g63)
    c: Coincident(g63,g51)
    c: Block(g61)
    c: Block(g60)
    c: Block(g62)
    c: Block(g63)
    c: Vertical(g64)
    c: Coincident(g64,g57)
    c: Vertical(g65)
    c: Coincident(g65,g56)
    c: Vertical(g66)
    c: Coincident(g66,g54)
    c: Vertical(g67)
    c: Coincident(g67,g53)
    c: Block(g64)
    c: Block(g65)
    c: Block(g66)
    c: Block(g67)
    c: Coincident(g68,g61)
    c: Coincident(g68,g60)
    c: Block(g68)
    c: Block(g69)
    c: Coincident(g69,g65)
    c: Block(g70)
    c: Coincident(g70,g67)
    c: Block(g71)
    c: Coincident(g71,g63)
